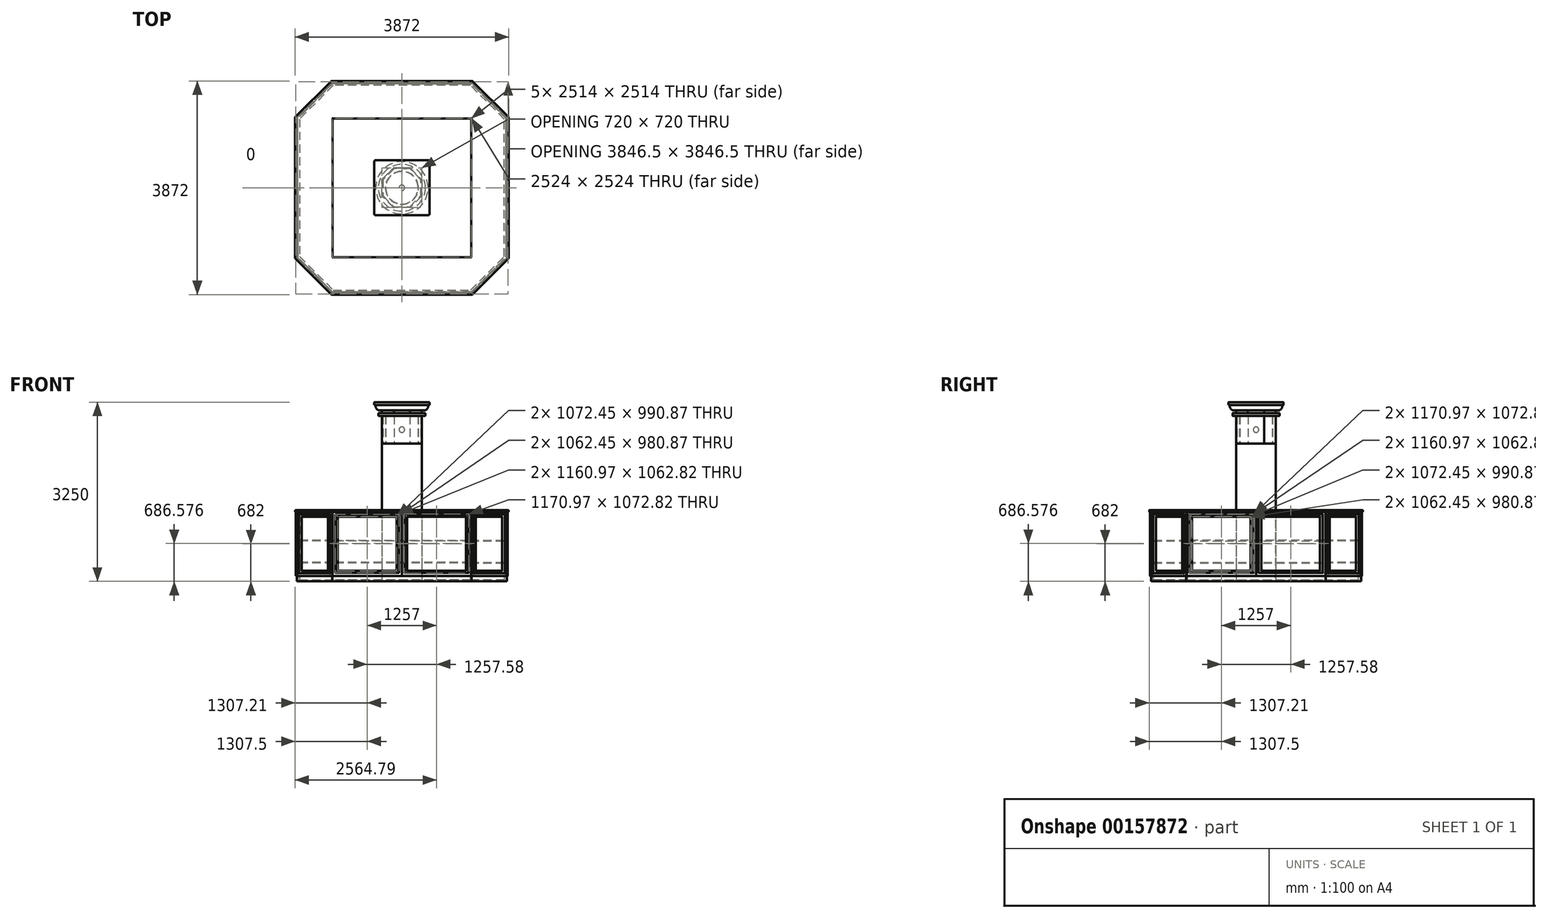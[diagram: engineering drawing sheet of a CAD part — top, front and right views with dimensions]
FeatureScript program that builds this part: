
annotation { "Feature Type Name" : "Feature", "Feature Type Description" : "" }
export const myFeature = defineFeature(function(context is Context, id is Id, definition is map)
    precondition{}
    {
        {
            var Q0;
            Q0=qCreatedBy(makeId("Top.planeOp"),FACE);
            var sketch = newSketch(context, id + "F0", { "sketchPlane" : qUnion([Q0])});
            skCircle(sketch, "E0.cCircle", {"center": v(0, 0) * mm, "radius": 360 * mm, "construction": true});
            skLineSegment(sketch, "E0.0", {"start": v(149.12, 360) * mm, "end": v(360, 149.12) * mm});
            skLineSegment(sketch, "E0.1", {"start": v(360, 149.12) * mm, "end": v(360, -149.12) * mm});
            skLineSegment(sketch, "E0.2", {"start": v(360, -149.12) * mm, "end": v(149.12, -360) * mm});
            skLineSegment(sketch, "E0.3", {"start": v(149.12, -360) * mm, "end": v(-149.12, -360) * mm});
            skLineSegment(sketch, "E0.4", {"start": v(-149.12, -360) * mm, "end": v(-360, -149.12) * mm});
            skLineSegment(sketch, "E0.5", {"start": v(-360, -149.12) * mm, "end": v(-360, 149.12) * mm});
            skLineSegment(sketch, "E0.6", {"start": v(-360, 149.12) * mm, "end": v(-149.12, 360) * mm});
            skLineSegment(sketch, "E0.7", {"start": v(-149.12, 360) * mm, "end": v(149.12, 360) * mm});
            skPoint(sketch, "E0.0.midPoint", {"position": v(254.56, 254.56) * mm});
            skLineSegment(sketch, "E1", {"start": v(0, 0) * mm, "end": v(360, 0) * mm, "construction": true});
            skSolve(sketch);
        }
        {
            var Q0;
            Q0=makeQuery(id+"F0.imprint","IMPRINT",FACE,{"disambiguationData":[TD([[makeQuery(id+"F0.imprint","IMPRINT",EDGE,{"derivedFrom":sQuery(id+"F0.wireOp",EDGE,"E0.0")}),-1.0]])]});
            var Q1;
            Q1=sQuery(id+"F0.wireOp",EDGE,"E1");
            extrude(context, id + "F1", {"entities" : qUnion([Q0]), "surfaceEntities" : qUnion([Q1]), "depth" : 3000 * mm});
        }
        {
            var Q0;
            Q0=qCreatedBy(makeId("Top.planeOp"),FACE);
            var sketch = newSketch(context, id + "F2", { "sketchPlane" : qUnion([Q0])});
            skLineSegment(sketch, "E2.bottom", {"start": v(1886, -1886) * mm, "end": v(-1886, -1886) * mm});
            skLineSegment(sketch, "E2.top", {"start": v(1886, 1886) * mm, "end": v(-1886, 1886) * mm});
            skLineSegment(sketch, "E2.left", {"start": v(1886, -1886) * mm, "end": v(1886, 1886) * mm});
            skLineSegment(sketch, "E2.right", {"start": v(-1886, -1886) * mm, "end": v(-1886, 1886) * mm});
            skPoint(sketch, "E2.middle", {"position": v(0, 0) * mm});
            skLineSegment(sketch, "E3.bottom", {"start": v(1257, -1257) * mm, "end": v(-1257, -1257) * mm});
            skLineSegment(sketch, "E3.top", {"start": v(1257, 1257) * mm, "end": v(-1257, 1257) * mm});
            skLineSegment(sketch, "E3.left", {"start": v(1257, -1257) * mm, "end": v(1257, 1257) * mm});
            skLineSegment(sketch, "E3.right", {"start": v(-1257, -1257) * mm, "end": v(-1257, 1257) * mm});
            skSolve(sketch);
        }
        {
            var Q0;
            Q0 = qSketchRegion(id + "F2", true);
            extrude(context, id + "F3", {"entities" : qUnion([Q0]), "depth" : 1264 * mm});
        }
        {
            var Q0;
            Q0=makeQuery(id+"F3.opExtrude","SWEPT_EDGE",EDGE,{"disambiguationData":[OSD([sQuery(id+"F2.wireOp",EDGE,"E2.top"),sQuery(id+"F2.wireOp",EDGE,"E2.right")])]});
            var Q1;
            Q1=makeQuery(id+"F3.opExtrude","SWEPT_EDGE",EDGE,{"disambiguationData":[OSD([sQuery(id+"F2.wireOp",EDGE,"E2.bottom"),sQuery(id+"F2.wireOp",EDGE,"E2.right")])]});
            var Q2;
            Q2=makeQuery(id+"F3.opExtrude","SWEPT_EDGE",EDGE,{"disambiguationData":[OSD([sQuery(id+"F2.wireOp",EDGE,"E2.bottom"),sQuery(id+"F2.wireOp",EDGE,"E2.left")])]});
            var Q3;
            Q3=makeQuery(id+"F3.opExtrude","SWEPT_EDGE",EDGE,{"disambiguationData":[OSD([sQuery(id+"F2.wireOp",EDGE,"E2.top"),sQuery(id+"F2.wireOp",EDGE,"E2.left")])]});
            chamfer(context, id + "F4", {"entities" : qUnion([Q0, Q1, Q2, Q3]), "width" : 629 * mm, "tangentPropagation" : true});
        }
        {
            var Q0;
            Q0=makeQuery(id+"F1.opExtrude","CAP_FACE",FACE,{"disambiguationData":[OSD([sQuery(id+"F0.wireOp",EDGE,"E0.0"),sQuery(id+"F0.wireOp",EDGE,"E0.1"),sQuery(id+"F0.wireOp",EDGE,"E0.2"),sQuery(id+"F0.wireOp",EDGE,"E0.3"),sQuery(id+"F0.wireOp",EDGE,"E0.4"),sQuery(id+"F0.wireOp",EDGE,"E0.5"),sQuery(id+"F0.wireOp",EDGE,"E0.6"),sQuery(id+"F0.wireOp",EDGE,"E0.7")])],"isStart":false});
            var sketch = newSketch(context, id + "F5", { "sketchPlane" : qUnion([Q0])});
            skCircle(sketch, "E4", {"center": v(0, 0) * mm, "radius": 425 * mm});
            skSolve(sketch);
        }
        {
            var Q0;
            Q0 = qSketchRegion(id + "F5", true);
            extrude(context, id + "F6", {"entities" : qUnion([Q0]), "operationType" : NewBodyOperationType.ADD, "depth" : 50 * mm});
        }
        {
            var Q0;
            Q0=makeQuery(id+"F6.opExtrude","CAP_FACE",FACE,{"disambiguationData":[OSD([sQuery(id+"F5.wireOp",EDGE,"E4")])],"isStart":false});
            var sketch = newSketch(context, id + "F7", { "sketchPlane" : qUnion([Q0])});
            skLineSegment(sketch, "E5.0.0", {"start": v(149.12, 360) * mm, "end": v(360, 149.12) * mm});
            skLineSegment(sketch, "E5.0.1", {"start": v(360, 149.12) * mm, "end": v(360, -149.12) * mm});
            skLineSegment(sketch, "E5.0.2", {"start": v(360, -149.12) * mm, "end": v(149.12, -360) * mm});
            skLineSegment(sketch, "E5.0.3", {"start": v(149.12, -360) * mm, "end": v(-149.12, -360) * mm});
            skLineSegment(sketch, "E5.0.4", {"start": v(-149.12, -360) * mm, "end": v(-360, -149.12) * mm});
            skLineSegment(sketch, "E5.0.5", {"start": v(-360, -149.12) * mm, "end": v(-360, 149.12) * mm});
            skLineSegment(sketch, "E5.0.6", {"start": v(-360, 149.12) * mm, "end": v(-149.12, 360) * mm});
            skLineSegment(sketch, "E5.0.7", {"start": v(-149.12, 360) * mm, "end": v(149.12, 360) * mm});
            skSolve(sketch);
        }
        {
            var Q0;
            Q0 = qSketchRegion(id + "F7", true);
            extrude(context, id + "F8", {"entities" : qUnion([Q0]), "operationType" : NewBodyOperationType.ADD, "depth" : 50 * mm});
        }
        {
            var Q0;
            Q0=makeQuery(id+"F8.opExtrude","CAP_FACE",FACE,{"disambiguationData":[OSD([sQuery(id+"F7.wireOp",EDGE,"E5.0.0"),sQuery(id+"F7.wireOp",EDGE,"E5.0.1"),sQuery(id+"F7.wireOp",EDGE,"E5.0.2"),sQuery(id+"F7.wireOp",EDGE,"E5.0.3"),sQuery(id+"F7.wireOp",EDGE,"E5.0.4"),sQuery(id+"F7.wireOp",EDGE,"E5.0.5"),sQuery(id+"F7.wireOp",EDGE,"E5.0.6"),sQuery(id+"F7.wireOp",EDGE,"E5.0.7")])],"isStart":false});
            var sketch = newSketch(context, id + "F9", { "sketchPlane" : qUnion([Q0])});
            skCircle(sketch, "E6", {"center": v(0, 0) * mm, "radius": 475 * mm});
            skSolve(sketch);
        }
        {
            var Q0;
            Q0 = qSketchRegion(id + "F9", true);
            extrude(context, id + "F10", {"entities" : qUnion([Q0]), "operationType" : NewBodyOperationType.ADD, "depth" : 100 * mm});
        }
        {
            var Q0;
            Q0=makeQuery(id+"F10.opExtrude","CAP_FACE",FACE,{"disambiguationData":[OSD([sQuery(id+"F9.wireOp",EDGE,"E6")])],"isStart":false});
            var sketch = newSketch(context, id + "F11", { "sketchPlane" : qUnion([Q0])});
            skLineSegment(sketch, "E7.bottom", {"start": v(500, -500) * mm, "end": v(-500, -500) * mm});
            skLineSegment(sketch, "E7.top", {"start": v(500, 500) * mm, "end": v(-500, 500) * mm});
            skLineSegment(sketch, "E7.left", {"start": v(500, -500) * mm, "end": v(500, 500) * mm});
            skLineSegment(sketch, "E7.right", {"start": v(-500, -500) * mm, "end": v(-500, 500) * mm});
            skPoint(sketch, "E7.middle", {"position": v(0, 0) * mm});
            skSolve(sketch);
        }
        {
            var Q0;
            Q0 = qSketchRegion(id + "F11", true);
            extrude(context, id + "F12", {"entities" : qUnion([Q0]), "operationType" : NewBodyOperationType.ADD, "depth" : 50 * mm});
        }
        {
            var Q0;
            Q0=makeQuery(id+"F10.opExtrude","CAP_EDGE",EDGE,{"disambiguationData":[OSD([sQuery(id+"F9.wireOp",EDGE,"E6")])],"isStart":true});
            fillet(context, id + "F13", {"entities" : qUnion([Q0]), "radius" : 75 * mm, "tangentPropagation" : true, "allowEdgeOverflow" : false});
        }
        {
            var Q0;
            Q0=makeQuery(id+"F12.opExtrude","SWEPT_EDGE",EDGE,{"disambiguationData":[OSD([sQuery(id+"F11.wireOp",EDGE,"E7.bottom"),sQuery(id+"F11.wireOp",EDGE,"E7.right")])]});
            var Q1;
            Q1=makeQuery(id+"F12.opExtrude","SWEPT_EDGE",EDGE,{"disambiguationData":[OSD([sQuery(id+"F11.wireOp",EDGE,"E7.bottom"),sQuery(id+"F11.wireOp",EDGE,"E7.left")])]});
            var Q2;
            Q2=makeQuery(id+"F12.opExtrude","SWEPT_EDGE",EDGE,{"disambiguationData":[OSD([sQuery(id+"F11.wireOp",EDGE,"E7.top"),sQuery(id+"F11.wireOp",EDGE,"E7.right")])]});
            var Q3;
            Q3=makeQuery(id+"F12.opExtrude","SWEPT_EDGE",EDGE,{"disambiguationData":[OSD([sQuery(id+"F11.wireOp",EDGE,"E7.top"),sQuery(id+"F11.wireOp",EDGE,"E7.left")])]});
            fillet(context, id + "F14", {"entities" : qUnion([Q0, Q1, Q2, Q3]), "radius" : 25 * mm, "tangentPropagation" : true, "allowEdgeOverflow" : false});
        }
        {
            var Q0;
            Q0=makeQuery(id+"F6.opExtrude","SWEPT_FACE",FACE,{"disambiguationData":[OSD([sQuery(id+"F5.wireOp",EDGE,"E4")])]});
            fillet(context, id + "F15", {"entities" : qUnion([Q0]), "radius" : 5 * mm, "tangentPropagation" : true, "allowEdgeOverflow" : false});
        }
        {
            var Q0;
            Q0=makeQuery(id+"F3.opExtrude","CAP_FACE",FACE,{"disambiguationData":[OSD([sQuery(id+"F2.wireOp",EDGE,"E2.bottom"),sQuery(id+"F2.wireOp",EDGE,"E2.top"),sQuery(id+"F2.wireOp",EDGE,"E2.left"),sQuery(id+"F2.wireOp",EDGE,"E2.right"),sQuery(id+"F2.wireOp",EDGE,"E3.bottom"),sQuery(id+"F2.wireOp",EDGE,"E3.top"),sQuery(id+"F2.wireOp",EDGE,"E3.left"),sQuery(id+"F2.wireOp",EDGE,"E3.right")])],"isStart":false});
            var sketch = newSketch(context, id + "F16", { "sketchPlane" : qUnion([Q0])});
            skLineSegment(sketch, "E8.0", {"start": v(1277.71, -1936) * mm, "end": v(1936, -1277.71) * mm});
            skLineSegment(sketch, "E8.1", {"start": v(1936, -1277.71) * mm, "end": v(1936, 1277.71) * mm});
            skLineSegment(sketch, "E8.2", {"start": v(1277.71, -1936) * mm, "end": v(-1277.71, -1936) * mm});
            skLineSegment(sketch, "E8.3", {"start": v(1936, 1277.71) * mm, "end": v(1277.71, 1936) * mm});
            skLineSegment(sketch, "E8.4", {"start": v(-1936, -1277.71) * mm, "end": v(-1277.71, -1936) * mm});
            skLineSegment(sketch, "E8.5", {"start": v(-1936, -1277.71) * mm, "end": v(-1936, 1277.71) * mm});
            skLineSegment(sketch, "E8.6", {"start": v(-1277.71, 1936) * mm, "end": v(-1936, 1277.71) * mm});
            skLineSegment(sketch, "E8.7", {"start": v(1277.71, 1936) * mm, "end": v(-1277.71, 1936) * mm});
            skLineSegment(sketch, "E9.0", {"start": v(1257, -1257) * mm, "end": v(1257, 1257) * mm});
            skLineSegment(sketch, "E9.1", {"start": v(1257, -1257) * mm, "end": v(-1257, -1257) * mm});
            skLineSegment(sketch, "E9.2", {"start": v(1257, 1257) * mm, "end": v(-1257, 1257) * mm});
            skLineSegment(sketch, "E9.3", {"start": v(-1257, -1257) * mm, "end": v(-1257, 1257) * mm});
            skSolve(sketch);
        }
        {
            var Q0;
            Q0=makeQuery(id+"F3.opExtrude","SWEPT_FACE",FACE,{"disambiguationData":[OSD([sQuery(id+"F2.wireOp",EDGE,"E3.top")])]});
            var Q1;
            Q1=makeQuery(id+"F3.opExtrude","SWEPT_FACE",FACE,{"disambiguationData":[OSD([sQuery(id+"F2.wireOp",EDGE,"E3.left")])]});
            var Q2;
            Q2=makeQuery(id+"F3.opExtrude","SWEPT_FACE",FACE,{"disambiguationData":[OSD([sQuery(id+"F2.wireOp",EDGE,"E3.bottom")])]});
            var Q3;
            Q3=makeQuery(id+"F3.opExtrude","SWEPT_FACE",FACE,{"disambiguationData":[OSD([sQuery(id+"F2.wireOp",EDGE,"E3.right")])]});
            shell(context, id + "F17", {"entities" : qUnion([Q0, Q1, Q2, Q3]), "thickness" : 30 * mm});
        }
        {
            var Q0;
            {var subQ0=sQuery(id+"F2.wireOp",EDGE,"E3.right");var subQ1=sQuery(id+"F2.wireOp",EDGE,"E3.left");var subQ2=sQuery(id+"F2.wireOp",EDGE,"E3.top");var subQ3=sQuery(id+"F2.wireOp",EDGE,"E3.bottom");var subQ4=sQuery(id+"F2.wireOp",EDGE,"E2.right");var subQ5=sQuery(id+"F2.wireOp",EDGE,"E2.left");var subQ6=sQuery(id+"F2.wireOp",EDGE,"E2.top");var subQ7=sQuery(id+"F2.wireOp",EDGE,"E2.bottom");Q0=makeQuery(id+"F17.opShell","OFFSET_FACE",FACE,{"disambiguationData":[OSD([subQ7,subQ6,subQ5,subQ4,subQ3,subQ2,subQ1,subQ0]),TDD([makeQuery(id+"F3.opExtrude","CAP_FACE",FACE,{"disambiguationData":[OSD([subQ7,subQ6,subQ5,subQ4,subQ3,subQ2,subQ1,subQ0])],"isStart":true})])]});}
            cPlane(context, id + "F18", {"entities" : qUnion([Q0]), "cplaneType" : CPlaneType.OFFSET, "offset" : 300 * mm, "width" : 150 * mm, "height" : 150 * mm});
        }
        {
            var Q0;
            Q0=qCreatedBy(id+"F18.planeOp",FACE);
            var sketch = newSketch(context, id + "F19", { "sketchPlane" : qUnion([Q0])});
            skLineSegment(sketch, "E10.0.0", {"start": v(1244.57, 1856) * mm, "end": v(-1244.57, 1856) * mm});
            skLineSegment(sketch, "E10.0.1", {"start": v(-1244.57, 1856) * mm, "end": v(-1856, 1244.57) * mm});
            skLineSegment(sketch, "E10.0.2", {"start": v(-1856, 1244.57) * mm, "end": v(-1856, -1244.57) * mm});
            skLineSegment(sketch, "E10.0.3", {"start": v(-1244.57, -1856) * mm, "end": v(-1856, -1244.57) * mm});
            skLineSegment(sketch, "E10.0.4", {"start": v(-1244.57, -1856) * mm, "end": v(1244.57, -1856) * mm});
            skLineSegment(sketch, "E10.0.5", {"start": v(1244.57, -1856) * mm, "end": v(1856, -1244.57) * mm});
            skLineSegment(sketch, "E10.0.6", {"start": v(1856, -1244.57) * mm, "end": v(1856, 1244.57) * mm});
            skLineSegment(sketch, "E10.0.7", {"start": v(1244.57, 1856) * mm, "end": v(1856, 1244.57) * mm});
            skLineSegment(sketch, "E11.0", {"start": v(1257, 1257) * mm, "end": v(-1257, 1257) * mm});
            skLineSegment(sketch, "E11.1", {"start": v(1257, -1257) * mm, "end": v(1257, 1257) * mm});
            skLineSegment(sketch, "E11.2", {"start": v(1257, -1257) * mm, "end": v(-1257, -1257) * mm});
            skLineSegment(sketch, "E11.3", {"start": v(-1257, -1257) * mm, "end": v(-1257, 1257) * mm});
            skSolve(sketch);
        }
        {
            var Q0;
            Q0 = qSketchRegion(id + "F19", true);
            extrude(context, id + "F20", {"entities" : qUnion([Q0]), "operationType" : NewBodyOperationType.ADD, "depth" : 15 * mm});
        }
        {
            var Q0;
            Q0=qCreatedBy(id+"F18.planeOp",FACE);
            cPlane(context, id + "F21", {"entities" : qUnion([Q0]), "cplaneType" : CPlaneType.OFFSET, "offset" : 400 * mm, "width" : 150 * mm, "height" : 150 * mm});
        }
        {
            var Q0;
            Q0=qCreatedBy(id+"F21.planeOp",FACE);
            var sketch = newSketch(context, id + "F22", { "sketchPlane" : qUnion([Q0])});
            skLineSegment(sketch, "E12.0.0", {"start": v(1856, 1244.57) * mm, "end": v(1244.57, 1856) * mm});
            skLineSegment(sketch, "E12.0.1", {"start": v(1244.57, 1856) * mm, "end": v(-1244.57, 1856) * mm});
            skLineSegment(sketch, "E12.0.2", {"start": v(-1244.57, 1856) * mm, "end": v(-1856, 1244.57) * mm});
            skLineSegment(sketch, "E12.0.3", {"start": v(-1856, 1244.57) * mm, "end": v(-1856, -1244.57) * mm});
            skLineSegment(sketch, "E12.0.4", {"start": v(-1856, -1244.57) * mm, "end": v(-1244.57, -1856) * mm});
            skLineSegment(sketch, "E12.0.5", {"start": v(-1244.57, -1856) * mm, "end": v(1244.57, -1856) * mm});
            skLineSegment(sketch, "E12.0.6", {"start": v(1244.57, -1856) * mm, "end": v(1856, -1244.57) * mm});
            skLineSegment(sketch, "E12.0.7", {"start": v(1856, -1244.57) * mm, "end": v(1856, 1244.57) * mm});
            skLineSegment(sketch, "E13.0", {"start": v(1257, 1257) * mm, "end": v(-1257, 1257) * mm});
            skLineSegment(sketch, "E13.1", {"start": v(1257, -1257) * mm, "end": v(1257, 1257) * mm});
            skLineSegment(sketch, "E13.2", {"start": v(1257, -1257) * mm, "end": v(-1257, -1257) * mm});
            skLineSegment(sketch, "E13.3", {"start": v(-1257, -1257) * mm, "end": v(-1257, 1257) * mm});
            skSolve(sketch);
        }
        {
            var Q0;
            Q0 = qSketchRegion(id + "F22", true);
            extrude(context, id + "F23", {"entities" : qUnion([Q0]), "operationType" : NewBodyOperationType.ADD, "depth" : 15 * mm});
        }
        {
            var Q0;
            Q0 = qSketchRegion(id + "F16", true);
            extrude(context, id + "F24", {"entities" : qUnion([Q0]), "depth" : 25 * mm});
        }
        {
            var Q0;
            Q0=makeQuery(id+"F3.opExtrude","CAP_FACE",FACE,{"disambiguationData":[OSD([sQuery(id+"F2.wireOp",EDGE,"E2.bottom"),sQuery(id+"F2.wireOp",EDGE,"E2.top"),sQuery(id+"F2.wireOp",EDGE,"E2.left"),sQuery(id+"F2.wireOp",EDGE,"E2.right"),sQuery(id+"F2.wireOp",EDGE,"E3.bottom"),sQuery(id+"F2.wireOp",EDGE,"E3.top"),sQuery(id+"F2.wireOp",EDGE,"E3.left"),sQuery(id+"F2.wireOp",EDGE,"E3.right")])],"isStart":true});
            var sketch = newSketch(context, id + "F25", { "sketchPlane" : qUnion([Q0])});
            skLineSegment(sketch, "E14.0", {"start": v(1257, 1257) * mm, "end": v(-1257, 1257) * mm});
            skLineSegment(sketch, "E14.1", {"start": v(1257, 1257) * mm, "end": v(1257, -1257) * mm});
            skLineSegment(sketch, "E14.2", {"start": v(1257, -1257) * mm, "end": v(-1257, -1257) * mm});
            skLineSegment(sketch, "E14.3", {"start": v(-1257, 1257) * mm, "end": v(-1257, -1257) * mm});
            skLineSegment(sketch, "E15.0", {"start": v(1906, 1265.28) * mm, "end": v(1906, -1265.28) * mm});
            skLineSegment(sketch, "E15.1", {"start": v(1265.28, -1906) * mm, "end": v(1906, -1265.28) * mm});
            skLineSegment(sketch, "E15.2", {"start": v(1906, 1265.28) * mm, "end": v(1265.28, 1906) * mm});
            skLineSegment(sketch, "E15.3", {"start": v(1265.28, -1906) * mm, "end": v(-1265.28, -1906) * mm});
            skLineSegment(sketch, "E15.4", {"start": v(1265.28, 1906) * mm, "end": v(-1265.28, 1906) * mm});
            skLineSegment(sketch, "E15.5", {"start": v(-1265.28, 1906) * mm, "end": v(-1906, 1265.28) * mm});
            skLineSegment(sketch, "E15.6", {"start": v(-1906, 1265.28) * mm, "end": v(-1906, -1265.28) * mm});
            skLineSegment(sketch, "E15.7", {"start": v(-1906, -1265.28) * mm, "end": v(-1265.28, -1906) * mm});
            skSolve(sketch);
        }
        {
            var Q0;
            Q0 = qSketchRegion(id + "F25", true);
            extrude(context, id + "F26", {"entities" : qUnion([Q0]), "oppositeDirection" : true, "depth" : 100 * mm});
        }
        {
            var Q0;
            Q0=makeQuery(id+"F6.opExtrude","CAP_FACE",FACE,{"disambiguationData":[OSD([sQuery(id+"F5.wireOp",EDGE,"E4")])],"isStart":true});
            var sketch = newSketch(context, id + "F27", { "sketchPlane" : qUnion([Q0])});
            skCircle(sketch, "E16.0", {"center": v(0, 0) * mm, "radius": 420 * mm});
            skSolve(sketch);
        }
        {
            var Q0;
            Q0 = qSketchRegion(id + "F27", true);
            extrude(context, id + "F28", {"entities" : qUnion([Q0]), "operationType" : NewBodyOperationType.REMOVE, "depth" : 500 * mm});
        }
        {
            var Q0;
            Q0=makeQuery(id+"F28.boolean.opBoolean","COPY",FACE,{"derivedFrom":makeQuery(id+"F28.opExtrude","CAP_FACE",FACE,{"disambiguationData":[OSD([sQuery(id+"F27.wireOp",EDGE,"E16.0")])],"isStart":false})});
            var sketch = newSketch(context, id + "F29", { "sketchPlane" : qUnion([Q0])});
            skCircle(sketch, "E17", {"center": v(0, 0) * mm, "radius": 300 * mm});
            skSolve(sketch);
        }
        {
            var Q0;
            Q0 = qSketchRegion(id + "F29", true);
            extrude(context, id + "F30", {"entities" : qUnion([Q0]), "depth" : 500 * mm});
        }
        {
            var Q0;
            Q0=makeQuery(id+"F30.opExtrude","CAP_FACE",FACE,{"disambiguationData":[OSD([sQuery(id+"F29.wireOp",EDGE,"E17")])],"isStart":true});
            var Q1;
            Q1=makeQuery(id+"F30.opExtrude","CAP_FACE",FACE,{"disambiguationData":[OSD([sQuery(id+"F29.wireOp",EDGE,"E17")])],"isStart":false});
            shell(context, id + "F31", {"entities" : qUnion([Q0, Q1]), "thickness" : 2 * mm});
        }
        {
            var Q0;
            Q0=makeQuery(id+"F28.boolean.opBoolean","COPY",FACE,{"derivedFrom":makeQuery(id+"F28.opExtrude","CAP_FACE",FACE,{"disambiguationData":[OSD([sQuery(id+"F27.wireOp",EDGE,"E16.0")])],"isStart":false})});
            var sketch = newSketch(context, id + "F32", { "sketchPlane" : qUnion([Q0])});
            skLineSegment(sketch, "E18.0", {"start": v(149.12, 360) * mm, "end": v(-149.12, 360) * mm});
            skLineSegment(sketch, "E19.0", {"start": v(-149.12, 360) * mm, "end": v(-360, 149.12) * mm});
            skLineSegment(sketch, "E20.0", {"start": v(-360, 149.12) * mm, "end": v(-360, -149.12) * mm});
            skLineSegment(sketch, "E21.0", {"start": v(360, 149.12) * mm, "end": v(149.12, 360) * mm});
            skLineSegment(sketch, "E22.0", {"start": v(360, -149.12) * mm, "end": v(360, 149.12) * mm});
            skLineSegment(sketch, "E23.0", {"start": v(149.12, -360) * mm, "end": v(360, -149.12) * mm});
            skLineSegment(sketch, "E24.0", {"start": v(-360, -149.12) * mm, "end": v(-149.12, -360) * mm});
            skLineSegment(sketch, "E25.0", {"start": v(-149.12, -360) * mm, "end": v(149.12, -360) * mm});
            skLineSegment(sketch, "E26.0", {"start": v(-345, 142.9) * mm, "end": v(-345, -142.9) * mm});
            skLineSegment(sketch, "E26.1", {"start": v(-142.9, 345) * mm, "end": v(-345, 142.9) * mm});
            skLineSegment(sketch, "E26.2", {"start": v(-345, -142.9) * mm, "end": v(-142.9, -345) * mm});
            skLineSegment(sketch, "E26.3", {"start": v(142.9, 345) * mm, "end": v(-142.9, 345) * mm});
            skLineSegment(sketch, "E26.4", {"start": v(-142.9, -345) * mm, "end": v(142.9, -345) * mm});
            skLineSegment(sketch, "E26.5", {"start": v(142.9, -345) * mm, "end": v(345, -142.9) * mm});
            skLineSegment(sketch, "E26.6", {"start": v(345, -142.9) * mm, "end": v(345, 142.9) * mm});
            skLineSegment(sketch, "E26.7", {"start": v(345, 142.9) * mm, "end": v(142.9, 345) * mm});
            skSolve(sketch);
        }
        {
            var Q0;
            Q0=makeQuery(id+"F32.imprint","IMPRINT",FACE,{"disambiguationData":[TD([[makeQuery(id+"F32.imprint","IMPRINT",EDGE,{"derivedFrom":sQuery(id+"F32.wireOp",EDGE,"E18.0")}),1.0]])]});
            extrude(context, id + "F33", {"entities" : qUnion([Q0]), "depth" : 500 * mm});
        }
        {
            var Q0;
            Q0=makeQuery(id+"F1.opExtrude","SWEPT_FACE",FACE,{"disambiguationData":[OSD([sQuery(id+"F0.wireOp",EDGE,"E0.7")])]});
            var sketch = newSketch(context, id + "F34", { "sketchPlane" : qUnion([Q0])});
            skLineSegment(sketch, "E27", {"start": v(-62.5, 2900) * mm, "end": v(-62.5, 100) * mm});
            skArc(sketch, "E28.0.startCap", {"start": v(-100, 2900) * mm, "mid": v(-62.5, 2937.5) * mm, "end": v(-25, 2900) * mm});
            skArc(sketch, "E28.0.endCap", {"start": v(-25, 100) * mm, "mid": v(-62.5, 62.5) * mm, "end": v(-100, 100) * mm});
            skLineSegment(sketch, "E28.0.left", {"start": v(-25, 2900) * mm, "end": v(-25, 100) * mm});
            skLineSegment(sketch, "E28.0.right", {"start": v(-100, 2900) * mm, "end": v(-100, 100) * mm});
            skSolve(sketch);
        }
        {
            var Q0;
            Q0 = qSketchRegion(id + "F34", true);
            extrude(context, id + "F35", {"entities" : qUnion([Q0]), "operationType" : NewBodyOperationType.REMOVE, "oppositeDirection" : true, "depth" : 10 * mm});
        }
        {
            var Q0;
            {var subQ0=sQuery(id+"F34.wireOp",EDGE,"E28.0.startCap");var subQ1=sQuery(id+"F34.wireOp",EDGE,"E28.0.right");Q0=makeQuery(id+"F35.boolean.opBoolean","COPY",EDGE,{"disambiguationData":[TD([makeQuery(id+"F35.opExtrude","SWEPT_FACE",FACE,{"disambiguationData":[OSD([subQ0])]})])],"derivedFrom":makeQuery(id+"F35.opExtrude","CAP_EDGE",EDGE,{"disambiguationData":[OSD([subQ1])],"isStart":false})});}
            var Q1;
            {var subQ0=sQuery(id+"F34.wireOp",EDGE,"E28.0.right");Q1=makeQuery(id+"F35.boolean.opBoolean","COPY",EDGE,{"disambiguationData":[TD([makeQuery(id+"F28.boolean.opBoolean","COPY",FACE,{"derivedFrom":makeQuery(id+"F28.opExtrude","CAP_FACE",FACE,{"disambiguationData":[OSD([sQuery(id+"F27.wireOp",EDGE,"E16.0")])],"isStart":false})})])],"derivedFrom":makeQuery(id+"F35.opExtrude","CAP_EDGE",EDGE,{"disambiguationData":[OSD([subQ0])],"isStart":false})});}
            fillet(context, id + "F36", {"entities" : qUnion([Q0, Q1]), "radius" : 10 * mm, "tangentPropagation" : true, "allowEdgeOverflow" : false});
        }
        {
            var Q0;
            Q0=qCreatedBy(makeId("Front.planeOp"),FACE);
            var sketch = newSketch(context, id + "F37", { "sketchPlane" : qUnion([Q0])});
            skLineSegment(sketch, "E29", {"start": v(0, 0) * mm, "end": v(0, 3766.95) * mm, "construction": true});
            skSolve(sketch);
        }
        {
            var Q0;
            Q0=qCreatedBy(makeId("Front.planeOp"),FACE);
            var sketch = newSketch(context, id + "F38", { "sketchPlane" : qUnion([Q0])});
            skArc(sketch, "E30", {"start": v(0, 2800) * mm, "mid": v(-50, 2750) * mm, "end": v(0, 2700) * mm});
            skLineSegment(sketch, "E31", {"start": v(0, 2800) * mm, "end": v(0, 2700) * mm});
            skSolve(sketch);
        }
        {
            var Q0;
            Q0=qCreatedBy(makeId("Front.planeOp"),FACE);
            var sketch = newSketch(context, id + "F39", { "sketchPlane" : qUnion([Q0])});
            skLineSegment(sketch, "E32", {"start": v(0, 2828.4) * mm, "end": v(0, 2674.55) * mm, "construction": true});
            skSolve(sketch);
        }
        {
            var Q0;
            Q0=makeQuery(id+"F38.imprint","IMPRINT",FACE,{"disambiguationData":[TD([[makeQuery(id+"F38.imprint","IMPRINT",EDGE,{"derivedFrom":sQuery(id+"F38.wireOp",EDGE,"E30")}),1.0]])]});
            var Q1;
            Q1=sQuery(id+"F39.wireOp",EDGE,"E32");
            revolve(context, id + "F40", {"entities" : qUnion([Q0]), "axis" : qUnion([Q1]), "revolveType" : RevolveType.FULL});
        }
        {
            var Q0;
            Q0=makeQuery(id+"F3.opExtrude","SWEPT_FACE",FACE,{"disambiguationData":[OSD([sQuery(id+"F2.wireOp",EDGE,"E2.left")])]});
            var sketch = newSketch(context, id + "F41", { "sketchPlane" : qUnion([Q0])});
            skLineSegment(sketch, "E33", {"start": v(0, 1264) * mm, "end": v(0, 100) * mm, "construction": true});
            skPoint(sketch, "E33.endSnap0", {"position": v(0, 1264) * mm});
            skLineSegment(sketch, "E34", {"start": v(0, 682) * mm, "end": v(-1257, 682) * mm, "construction": true});
            skLineSegment(sketch, "E35.bottom", {"start": v(0, 100) * mm, "end": v(-1257, 100) * mm});
            skLineSegment(sketch, "E35.top", {"start": v(0, 1264) * mm, "end": v(-1257, 1264) * mm});
            skLineSegment(sketch, "E35.left", {"start": v(0, 100) * mm, "end": v(0, 1264) * mm});
            skLineSegment(sketch, "E35.right", {"start": v(-1257, 100) * mm, "end": v(-1257, 1264) * mm});
            skPoint(sketch, "E35.middle", {"position": v(-628.5, 682) * mm});
            skLineSegment(sketch, "E36.bottom", {"start": v(-97.27, 191.57) * mm, "end": v(-1159.73, 191.57) * mm});
            skLineSegment(sketch, "E36.top", {"start": v(-97.27, 1172.43) * mm, "end": v(-1159.73, 1172.43) * mm});
            skLineSegment(sketch, "E36.left", {"start": v(-97.27, 191.57) * mm, "end": v(-97.27, 1172.43) * mm});
            skLineSegment(sketch, "E36.right", {"start": v(-1159.73, 191.57) * mm, "end": v(-1159.73, 1172.43) * mm});
            skSolve(sketch);
        }
        {
            var Q0;
            Q0 = qSketchRegion(id + "F41", true);
            extrude(context, id + "F42", {"entities" : qUnion([Q0]), "depth" : 10 * mm});
        }
        {
            var Q0;
            Q0=makeQuery(id+"F42.opExtrude","CAP_FACE",FACE,{"disambiguationData":[OSD([sQuery(id+"F41.wireOp",EDGE,"E35.bottom"),sQuery(id+"F41.wireOp",EDGE,"E35.top"),sQuery(id+"F41.wireOp",EDGE,"E35.left"),sQuery(id+"F41.wireOp",EDGE,"E35.right"),sQuery(id+"F41.wireOp",EDGE,"E36.bottom"),sQuery(id+"F41.wireOp",EDGE,"E36.top"),sQuery(id+"F41.wireOp",EDGE,"E36.left"),sQuery(id+"F41.wireOp",EDGE,"E36.right")])],"isStart":false});
            var sketch = newSketch(context, id + "F43", { "sketchPlane" : qUnion([Q0])});
            skLineSegment(sketch, "E37.bottom", {"start": v(-1257, 1264) * mm, "end": v(0, 1264) * mm});
            skLineSegment(sketch, "E37.top", {"start": v(-1257, 100) * mm, "end": v(0, 100) * mm});
            skLineSegment(sketch, "E37.left", {"start": v(-1257, 1264) * mm, "end": v(-1257, 100) * mm});
            skLineSegment(sketch, "E37.right", {"start": v(0, 1264) * mm, "end": v(0, 100) * mm});
            skLineSegment(sketch, "E38.bottom", {"start": v(-1209.28, 1217.98) * mm, "end": v(-48.3, 1217.98) * mm});
            skLineSegment(sketch, "E38.top", {"start": v(-1209.28, 155.17) * mm, "end": v(-48.3, 155.17) * mm});
            skLineSegment(sketch, "E38.left", {"start": v(-1209.28, 1217.98) * mm, "end": v(-1209.28, 155.17) * mm});
            skLineSegment(sketch, "E38.right", {"start": v(-48.3, 1217.98) * mm, "end": v(-48.3, 155.17) * mm});
            skSolve(sketch);
        }
        {
            var Q0;
            Q0 = qSketchRegion(id + "F43", true);
            extrude(context, id + "F44", {"entities" : qUnion([Q0]), "depth" : 25 * mm});
        }
        {
            var Q0;
            Q0=makeQuery(id+"F3.opExtrude","SWEPT_FACE",FACE,{"disambiguationData":[OSD([sQuery(id+"F2.wireOp",EDGE,"E2.left")])]});
            var sketch = newSketch(context, id + "F45", { "sketchPlane" : qUnion([Q0])});
            skLineSegment(sketch, "E39.0", {"start": v(-97.27, 1172.43) * mm, "end": v(-1159.73, 1172.43) * mm});
            skLineSegment(sketch, "E39.1", {"start": v(-1159.73, 191.57) * mm, "end": v(-1159.73, 1172.43) * mm});
            skLineSegment(sketch, "E39.2", {"start": v(-97.27, 191.57) * mm, "end": v(-97.27, 1172.43) * mm});
            skLineSegment(sketch, "E39.3", {"start": v(-97.27, 191.57) * mm, "end": v(-1159.73, 191.57) * mm});
            skSolve(sketch);
        }
        {
            var Q0;
            Q0 = qSketchRegion(id + "F45", true);
            extrude(context, id + "F46", {"entities" : qUnion([Q0]), "depth" : 5 * mm});
        }
        {
            var Q0;
            Q0=makeQuery(id+"F46.opExtrude","SWEPT_BODY",BODY,{"disambiguationData":[OSD([sQuery(id+"F45.wireOp",EDGE,"E39.0"),sQuery(id+"F45.wireOp",EDGE,"E39.1"),sQuery(id+"F45.wireOp",EDGE,"E39.2"),sQuery(id+"F45.wireOp",EDGE,"E39.3")])]});
            var Q1;
            Q1=makeQuery(id+"F42.opExtrude","SWEPT_BODY",BODY,{"disambiguationData":[OSD([sQuery(id+"F41.wireOp",EDGE,"E35.bottom"),sQuery(id+"F41.wireOp",EDGE,"E35.top"),sQuery(id+"F41.wireOp",EDGE,"E35.left"),sQuery(id+"F41.wireOp",EDGE,"E35.right"),sQuery(id+"F41.wireOp",EDGE,"E36.bottom"),sQuery(id+"F41.wireOp",EDGE,"E36.top"),sQuery(id+"F41.wireOp",EDGE,"E36.left"),sQuery(id+"F41.wireOp",EDGE,"E36.right")])]});
            var Q2;
            Q2=makeQuery(id+"F44.opExtrude","SWEPT_BODY",BODY,{"disambiguationData":[OSD([sQuery(id+"F43.wireOp",EDGE,"E37.bottom"),sQuery(id+"F43.wireOp",EDGE,"E37.top"),sQuery(id+"F43.wireOp",EDGE,"E37.left"),sQuery(id+"F43.wireOp",EDGE,"E37.right"),sQuery(id+"F43.wireOp",EDGE,"E38.bottom"),sQuery(id+"F43.wireOp",EDGE,"E38.top"),sQuery(id+"F43.wireOp",EDGE,"E38.left"),sQuery(id+"F43.wireOp",EDGE,"E38.right")])]});
            var Q3;
            Q3=qCreatedBy(makeId("Front.planeOp"),FACE);
            mirror(context, id + "F47", {"entities" : qUnion([Q0, Q1, Q2]), "mirrorPlane" : qUnion([Q3])});
        }
        {
            var Q0;
            Q0=qCreatedBy(makeId("Front.planeOp"),FACE);
            var sketch = newSketch(context, id + "F48", { "sketchPlane" : qUnion([Q0])});
            skLineSegment(sketch, "E40", {"start": v(0, 3551.4) * mm, "end": v(0, -1302.8) * mm, "construction": true});
            skSolve(sketch);
        }
        {
            var Q0;
            Q0=makeQuery(id+"F46.opExtrude","SWEPT_BODY",BODY,{"disambiguationData":[OSD([sQuery(id+"F45.wireOp",EDGE,"E39.0"),sQuery(id+"F45.wireOp",EDGE,"E39.1"),sQuery(id+"F45.wireOp",EDGE,"E39.2"),sQuery(id+"F45.wireOp",EDGE,"E39.3")])]});
            var Q1;
            Q1=makeQuery(id+"F42.opExtrude","SWEPT_BODY",BODY,{"disambiguationData":[OSD([sQuery(id+"F41.wireOp",EDGE,"E35.bottom"),sQuery(id+"F41.wireOp",EDGE,"E35.top"),sQuery(id+"F41.wireOp",EDGE,"E35.left"),sQuery(id+"F41.wireOp",EDGE,"E35.right"),sQuery(id+"F41.wireOp",EDGE,"E36.bottom"),sQuery(id+"F41.wireOp",EDGE,"E36.top"),sQuery(id+"F41.wireOp",EDGE,"E36.left"),sQuery(id+"F41.wireOp",EDGE,"E36.right")])]});
            var Q2;
            Q2=makeQuery(id+"F44.opExtrude","SWEPT_BODY",BODY,{"disambiguationData":[OSD([sQuery(id+"F43.wireOp",EDGE,"E37.bottom"),sQuery(id+"F43.wireOp",EDGE,"E37.top"),sQuery(id+"F43.wireOp",EDGE,"E37.left"),sQuery(id+"F43.wireOp",EDGE,"E37.right"),sQuery(id+"F43.wireOp",EDGE,"E38.bottom"),sQuery(id+"F43.wireOp",EDGE,"E38.top"),sQuery(id+"F43.wireOp",EDGE,"E38.left"),sQuery(id+"F43.wireOp",EDGE,"E38.right")])]});
            var Q3;
            Q3=makeQuery(id+"F47.opPattern","COPY",BODY,{"derivedFrom":makeQuery(id+"F44.opExtrude","SWEPT_BODY",BODY,{"disambiguationData":[OSD([sQuery(id+"F43.wireOp",EDGE,"E37.bottom"),sQuery(id+"F43.wireOp",EDGE,"E37.top"),sQuery(id+"F43.wireOp",EDGE,"E37.left"),sQuery(id+"F43.wireOp",EDGE,"E37.right"),sQuery(id+"F43.wireOp",EDGE,"E38.bottom"),sQuery(id+"F43.wireOp",EDGE,"E38.top"),sQuery(id+"F43.wireOp",EDGE,"E38.left"),sQuery(id+"F43.wireOp",EDGE,"E38.right")])]}),"instanceName":"1"});
            var Q4;
            Q4=makeQuery(id+"F47.opPattern","COPY",BODY,{"derivedFrom":makeQuery(id+"F42.opExtrude","SWEPT_BODY",BODY,{"disambiguationData":[OSD([sQuery(id+"F41.wireOp",EDGE,"E35.bottom"),sQuery(id+"F41.wireOp",EDGE,"E35.top"),sQuery(id+"F41.wireOp",EDGE,"E35.left"),sQuery(id+"F41.wireOp",EDGE,"E35.right"),sQuery(id+"F41.wireOp",EDGE,"E36.bottom"),sQuery(id+"F41.wireOp",EDGE,"E36.top"),sQuery(id+"F41.wireOp",EDGE,"E36.left"),sQuery(id+"F41.wireOp",EDGE,"E36.right")])]}),"instanceName":"1"});
            var Q5;
            Q5=makeQuery(id+"F47.opPattern","COPY",BODY,{"derivedFrom":makeQuery(id+"F46.opExtrude","SWEPT_BODY",BODY,{"disambiguationData":[OSD([sQuery(id+"F45.wireOp",EDGE,"E39.0"),sQuery(id+"F45.wireOp",EDGE,"E39.1"),sQuery(id+"F45.wireOp",EDGE,"E39.2"),sQuery(id+"F45.wireOp",EDGE,"E39.3")])]}),"instanceName":"1"});
            var Q6;
            Q6=sQuery(id+"F48.wireOp",EDGE,"E40");
            circularPattern(context, id + "F49", {"entities" : qUnion([Q0, Q1, Q2, Q3, Q4, Q5]), "axis" : qUnion([Q6]), "angle" : 360 * degree, "instanceCount" : 4, "equalSpace" : true});
        }
        {
            var Q0;
            Q0=makeQuery(id+"F4.opChamfer","BLEND_FACE",FACE,{"disambiguationData":[OSD([sQuery(id+"F2.wireOp",EDGE,"E2.bottom"),sQuery(id+"F2.wireOp",EDGE,"E2.left")])]});
            var sketch = newSketch(context, id + "F50", { "sketchPlane" : qUnion([Q0])});
            skLineSegment(sketch, "E41.bottom", {"start": v(-444.77, 1264) * mm, "end": v(444.77, 1264) * mm});
            skLineSegment(sketch, "E41.top", {"start": v(-444.77, 100) * mm, "end": v(444.77, 100) * mm});
            skLineSegment(sketch, "E41.left", {"start": v(-444.77, 1264) * mm, "end": v(-444.77, 100) * mm});
            skLineSegment(sketch, "E41.right", {"start": v(444.77, 1264) * mm, "end": v(444.77, 100) * mm});
            skLineSegment(sketch, "E42.bottom", {"start": v(337.74, 191.57) * mm, "end": v(-337.74, 191.57) * mm});
            skLineSegment(sketch, "E42.top", {"start": v(337.74, 1172.43) * mm, "end": v(-337.74, 1172.43) * mm});
            skLineSegment(sketch, "E42.left", {"start": v(337.74, 191.57) * mm, "end": v(337.74, 1172.43) * mm});
            skLineSegment(sketch, "E42.right", {"start": v(-337.74, 191.57) * mm, "end": v(-337.74, 1172.43) * mm});
            skPoint(sketch, "E42.middle", {"position": v(0, 682) * mm});
            skPoint(sketch, "E42.middle.positionSnap0", {"position": v(0, 1264) * mm});
            skPoint(sketch, "E42.middle.positionSnap1", {"position": v(-444.77, 682) * mm});
            skPoint(sketch, "E42.centerSnap0", {"position": v(0, 1264) * mm});
            skPoint(sketch, "E42.centerSnap1", {"position": v(-444.77, 682) * mm});
            skSolve(sketch);
        }
        {
            var Q0;
            Q0 = qSketchRegion(id + "F50", true);
            extrude(context, id + "F51", {"entities" : qUnion([Q0]), "depth" : 10 * mm});
        }
        {
            var Q0;
            Q0=makeQuery(id+"F51.opExtrude","CAP_FACE",FACE,{"disambiguationData":[OSD([sQuery(id+"F50.wireOp",EDGE,"E41.bottom"),sQuery(id+"F50.wireOp",EDGE,"E41.top"),sQuery(id+"F50.wireOp",EDGE,"E41.left"),sQuery(id+"F50.wireOp",EDGE,"E41.right"),sQuery(id+"F50.wireOp",EDGE,"E42.bottom"),sQuery(id+"F50.wireOp",EDGE,"E42.top"),sQuery(id+"F50.wireOp",EDGE,"E42.left"),sQuery(id+"F50.wireOp",EDGE,"E42.right")])],"isStart":false});
            var sketch = newSketch(context, id + "F52", { "sketchPlane" : qUnion([Q0])});
            skLineSegment(sketch, "E43.0", {"start": v(-444.77, 100) * mm, "end": v(-444.77, 1264) * mm});
            skLineSegment(sketch, "E43.1", {"start": v(-444.77, 1264) * mm, "end": v(444.77, 1264) * mm});
            skLineSegment(sketch, "E43.2", {"start": v(444.77, 1264) * mm, "end": v(444.77, 100) * mm});
            skLineSegment(sketch, "E43.3", {"start": v(-444.77, 100) * mm, "end": v(444.77, 100) * mm});
            skLineSegment(sketch, "E44.bottom", {"start": v(403.74, 146.02) * mm, "end": v(-403.74, 146.02) * mm});
            skLineSegment(sketch, "E44.top", {"start": v(403.74, 1217.98) * mm, "end": v(-403.74, 1217.98) * mm});
            skLineSegment(sketch, "E44.left", {"start": v(403.74, 146.02) * mm, "end": v(403.74, 1217.98) * mm});
            skLineSegment(sketch, "E44.right", {"start": v(-403.74, 146.02) * mm, "end": v(-403.74, 1217.98) * mm});
            skPoint(sketch, "E44.middle", {"position": v(0, 682) * mm});
            skPoint(sketch, "E44.middle.positionSnap0", {"position": v(-337.74, 682) * mm});
            skPoint(sketch, "E44.centerSnap0", {"position": v(-337.74, 682) * mm});
            skSolve(sketch);
        }
        {
            var Q0;
            Q0 = qSketchRegion(id + "F52", true);
            extrude(context, id + "F53", {"entities" : qUnion([Q0]), "depth" : 25 * mm});
        }
        {
            var Q0;
            Q0=makeQuery(id+"F4.opChamfer","BLEND_FACE",FACE,{"disambiguationData":[OSD([sQuery(id+"F2.wireOp",EDGE,"E2.bottom"),sQuery(id+"F2.wireOp",EDGE,"E2.left")])]});
            var sketch = newSketch(context, id + "F54", { "sketchPlane" : qUnion([Q0])});
            skLineSegment(sketch, "E45.0", {"start": v(337.74, 1172.43) * mm, "end": v(-337.74, 1172.43) * mm});
            skLineSegment(sketch, "E46.0", {"start": v(-337.74, 191.57) * mm, "end": v(-337.74, 1172.43) * mm});
            skLineSegment(sketch, "E47.0", {"start": v(337.74, 191.57) * mm, "end": v(337.74, 1172.43) * mm});
            skLineSegment(sketch, "E48.0", {"start": v(337.74, 191.57) * mm, "end": v(-337.74, 191.57) * mm});
            skSolve(sketch);
        }
        {
            var Q0;
            Q0 = qSketchRegion(id + "F54", true);
            extrude(context, id + "F55", {"entities" : qUnion([Q0]), "depth" : 5 * mm});
        }
        {
            var Q0;
            Q0=makeQuery(id+"F53.opExtrude","CAP_FACE",FACE,{"disambiguationData":[OSD([sQuery(id+"F52.wireOp",EDGE,"E43.0"),sQuery(id+"F52.wireOp",EDGE,"E43.1"),sQuery(id+"F52.wireOp",EDGE,"E43.2"),sQuery(id+"F52.wireOp",EDGE,"E43.3"),sQuery(id+"F52.wireOp",EDGE,"E44.bottom"),sQuery(id+"F52.wireOp",EDGE,"E44.top"),sQuery(id+"F52.wireOp",EDGE,"E44.left"),sQuery(id+"F52.wireOp",EDGE,"E44.right")])],"isStart":false});
            var Q1;
            Q1=makeQuery(id+"F51.opExtrude","CAP_FACE",FACE,{"disambiguationData":[OSD([sQuery(id+"F50.wireOp",EDGE,"E41.bottom"),sQuery(id+"F50.wireOp",EDGE,"E41.top"),sQuery(id+"F50.wireOp",EDGE,"E41.left"),sQuery(id+"F50.wireOp",EDGE,"E41.right"),sQuery(id+"F50.wireOp",EDGE,"E42.bottom"),sQuery(id+"F50.wireOp",EDGE,"E42.top"),sQuery(id+"F50.wireOp",EDGE,"E42.left"),sQuery(id+"F50.wireOp",EDGE,"E42.right")])],"isStart":false});
            var Q2;
            Q2=makeQuery(id+"F49.opPattern","COPY",FACE,{"derivedFrom":makeQuery(id+"F47.opPattern","COPY",FACE,{"derivedFrom":makeQuery(id+"F42.opExtrude","CAP_FACE",FACE,{"disambiguationData":[OSD([sQuery(id+"F41.wireOp",EDGE,"E35.bottom"),sQuery(id+"F41.wireOp",EDGE,"E35.top"),sQuery(id+"F41.wireOp",EDGE,"E35.left"),sQuery(id+"F41.wireOp",EDGE,"E35.right"),sQuery(id+"F41.wireOp",EDGE,"E36.bottom"),sQuery(id+"F41.wireOp",EDGE,"E36.top"),sQuery(id+"F41.wireOp",EDGE,"E36.left"),sQuery(id+"F41.wireOp",EDGE,"E36.right")])],"isStart":false}),"instanceName":"1"}),"instanceName":"1"});
            var Q3;
            Q3=makeQuery(id+"F49.opPattern","COPY",FACE,{"derivedFrom":makeQuery(id+"F47.opPattern","COPY",FACE,{"derivedFrom":makeQuery(id+"F44.opExtrude","CAP_FACE",FACE,{"disambiguationData":[OSD([sQuery(id+"F43.wireOp",EDGE,"E37.bottom"),sQuery(id+"F43.wireOp",EDGE,"E37.top"),sQuery(id+"F43.wireOp",EDGE,"E37.left"),sQuery(id+"F43.wireOp",EDGE,"E37.right"),sQuery(id+"F43.wireOp",EDGE,"E38.bottom"),sQuery(id+"F43.wireOp",EDGE,"E38.top"),sQuery(id+"F43.wireOp",EDGE,"E38.left"),sQuery(id+"F43.wireOp",EDGE,"E38.right")])],"isStart":false}),"instanceName":"1"}),"instanceName":"1"});
            var Q4;
            Q4=makeQuery(id+"F49.opPattern","COPY",EDGE,{"derivedFrom":makeQuery(id+"F47.opPattern","COPY",EDGE,{"derivedFrom":makeQuery(id+"F44.opExtrude","CAP_EDGE",EDGE,{"disambiguationData":[OSD([sQuery(id+"F43.wireOp",EDGE,"E37.right")])],"isStart":false}),"instanceName":"1"}),"instanceName":"1"});
            var Q5;
            Q5=makeQuery(id+"F49.opPattern","COPY",FACE,{"derivedFrom":makeQuery(id+"F42.opExtrude","CAP_FACE",FACE,{"disambiguationData":[OSD([sQuery(id+"F41.wireOp",EDGE,"E35.bottom"),sQuery(id+"F41.wireOp",EDGE,"E35.top"),sQuery(id+"F41.wireOp",EDGE,"E35.left"),sQuery(id+"F41.wireOp",EDGE,"E35.right"),sQuery(id+"F41.wireOp",EDGE,"E36.bottom"),sQuery(id+"F41.wireOp",EDGE,"E36.top"),sQuery(id+"F41.wireOp",EDGE,"E36.left"),sQuery(id+"F41.wireOp",EDGE,"E36.right")])],"isStart":false}),"instanceName":"1"});
            var Q6;
            Q6=makeQuery(id+"F49.opPattern","COPY",FACE,{"derivedFrom":makeQuery(id+"F47.opPattern","COPY",FACE,{"derivedFrom":makeQuery(id+"F44.opExtrude","CAP_FACE",FACE,{"disambiguationData":[OSD([sQuery(id+"F43.wireOp",EDGE,"E37.bottom"),sQuery(id+"F43.wireOp",EDGE,"E37.top"),sQuery(id+"F43.wireOp",EDGE,"E37.left"),sQuery(id+"F43.wireOp",EDGE,"E37.right"),sQuery(id+"F43.wireOp",EDGE,"E38.bottom"),sQuery(id+"F43.wireOp",EDGE,"E38.top"),sQuery(id+"F43.wireOp",EDGE,"E38.left"),sQuery(id+"F43.wireOp",EDGE,"E38.right")])],"isStart":false}),"instanceName":"1"}),"instanceName":"2"});
            var Q7;
            Q7=makeQuery(id+"F49.opPattern","COPY",FACE,{"derivedFrom":makeQuery(id+"F47.opPattern","COPY",FACE,{"derivedFrom":makeQuery(id+"F42.opExtrude","CAP_FACE",FACE,{"disambiguationData":[OSD([sQuery(id+"F41.wireOp",EDGE,"E35.bottom"),sQuery(id+"F41.wireOp",EDGE,"E35.top"),sQuery(id+"F41.wireOp",EDGE,"E35.left"),sQuery(id+"F41.wireOp",EDGE,"E35.right"),sQuery(id+"F41.wireOp",EDGE,"E36.bottom"),sQuery(id+"F41.wireOp",EDGE,"E36.top"),sQuery(id+"F41.wireOp",EDGE,"E36.left"),sQuery(id+"F41.wireOp",EDGE,"E36.right")])],"isStart":false}),"instanceName":"1"}),"instanceName":"2"});
            var Q8;
            Q8=makeQuery(id+"F49.opPattern","COPY",FACE,{"derivedFrom":makeQuery(id+"F42.opExtrude","CAP_FACE",FACE,{"disambiguationData":[OSD([sQuery(id+"F41.wireOp",EDGE,"E35.bottom"),sQuery(id+"F41.wireOp",EDGE,"E35.top"),sQuery(id+"F41.wireOp",EDGE,"E35.left"),sQuery(id+"F41.wireOp",EDGE,"E35.right"),sQuery(id+"F41.wireOp",EDGE,"E36.bottom"),sQuery(id+"F41.wireOp",EDGE,"E36.top"),sQuery(id+"F41.wireOp",EDGE,"E36.left"),sQuery(id+"F41.wireOp",EDGE,"E36.right")])],"isStart":false}),"instanceName":"2"});
            var Q9;
            Q9=makeQuery(id+"F49.opPattern","COPY",FACE,{"derivedFrom":makeQuery(id+"F44.opExtrude","CAP_FACE",FACE,{"disambiguationData":[OSD([sQuery(id+"F43.wireOp",EDGE,"E37.bottom"),sQuery(id+"F43.wireOp",EDGE,"E37.top"),sQuery(id+"F43.wireOp",EDGE,"E37.left"),sQuery(id+"F43.wireOp",EDGE,"E37.right"),sQuery(id+"F43.wireOp",EDGE,"E38.bottom"),sQuery(id+"F43.wireOp",EDGE,"E38.top"),sQuery(id+"F43.wireOp",EDGE,"E38.left"),sQuery(id+"F43.wireOp",EDGE,"E38.right")])],"isStart":false}),"instanceName":"2"});
            var Q10;
            Q10=makeQuery(id+"F49.opPattern","COPY",FACE,{"derivedFrom":makeQuery(id+"F47.opPattern","COPY",FACE,{"derivedFrom":makeQuery(id+"F44.opExtrude","CAP_FACE",FACE,{"disambiguationData":[OSD([sQuery(id+"F43.wireOp",EDGE,"E37.bottom"),sQuery(id+"F43.wireOp",EDGE,"E37.top"),sQuery(id+"F43.wireOp",EDGE,"E37.left"),sQuery(id+"F43.wireOp",EDGE,"E37.right"),sQuery(id+"F43.wireOp",EDGE,"E38.bottom"),sQuery(id+"F43.wireOp",EDGE,"E38.top"),sQuery(id+"F43.wireOp",EDGE,"E38.left"),sQuery(id+"F43.wireOp",EDGE,"E38.right")])],"isStart":false}),"instanceName":"1"}),"instanceName":"3"});
            var Q11;
            Q11=makeQuery(id+"F49.opPattern","COPY",FACE,{"derivedFrom":makeQuery(id+"F47.opPattern","COPY",FACE,{"derivedFrom":makeQuery(id+"F42.opExtrude","CAP_FACE",FACE,{"disambiguationData":[OSD([sQuery(id+"F41.wireOp",EDGE,"E35.bottom"),sQuery(id+"F41.wireOp",EDGE,"E35.top"),sQuery(id+"F41.wireOp",EDGE,"E35.left"),sQuery(id+"F41.wireOp",EDGE,"E35.right"),sQuery(id+"F41.wireOp",EDGE,"E36.bottom"),sQuery(id+"F41.wireOp",EDGE,"E36.top"),sQuery(id+"F41.wireOp",EDGE,"E36.left"),sQuery(id+"F41.wireOp",EDGE,"E36.right")])],"isStart":false}),"instanceName":"1"}),"instanceName":"3"});
            var Q12;
            Q12=makeQuery(id+"F49.opPattern","COPY",FACE,{"derivedFrom":makeQuery(id+"F42.opExtrude","CAP_FACE",FACE,{"disambiguationData":[OSD([sQuery(id+"F41.wireOp",EDGE,"E35.bottom"),sQuery(id+"F41.wireOp",EDGE,"E35.top"),sQuery(id+"F41.wireOp",EDGE,"E35.left"),sQuery(id+"F41.wireOp",EDGE,"E35.right"),sQuery(id+"F41.wireOp",EDGE,"E36.bottom"),sQuery(id+"F41.wireOp",EDGE,"E36.top"),sQuery(id+"F41.wireOp",EDGE,"E36.left"),sQuery(id+"F41.wireOp",EDGE,"E36.right")])],"isStart":false}),"instanceName":"3"});
            var Q13;
            Q13=makeQuery(id+"F49.opPattern","COPY",FACE,{"derivedFrom":makeQuery(id+"F44.opExtrude","CAP_FACE",FACE,{"disambiguationData":[OSD([sQuery(id+"F43.wireOp",EDGE,"E37.bottom"),sQuery(id+"F43.wireOp",EDGE,"E37.top"),sQuery(id+"F43.wireOp",EDGE,"E37.left"),sQuery(id+"F43.wireOp",EDGE,"E37.right"),sQuery(id+"F43.wireOp",EDGE,"E38.bottom"),sQuery(id+"F43.wireOp",EDGE,"E38.top"),sQuery(id+"F43.wireOp",EDGE,"E38.left"),sQuery(id+"F43.wireOp",EDGE,"E38.right")])],"isStart":false}),"instanceName":"3"});
            var Q14;
            Q14=makeQuery(id+"F42.opExtrude","CAP_FACE",FACE,{"disambiguationData":[OSD([sQuery(id+"F41.wireOp",EDGE,"E35.bottom"),sQuery(id+"F41.wireOp",EDGE,"E35.top"),sQuery(id+"F41.wireOp",EDGE,"E35.left"),sQuery(id+"F41.wireOp",EDGE,"E35.right"),sQuery(id+"F41.wireOp",EDGE,"E36.bottom"),sQuery(id+"F41.wireOp",EDGE,"E36.top"),sQuery(id+"F41.wireOp",EDGE,"E36.left"),sQuery(id+"F41.wireOp",EDGE,"E36.right")])],"isStart":false});
            var Q15;
            Q15=makeQuery(id+"F44.opExtrude","CAP_FACE",FACE,{"disambiguationData":[OSD([sQuery(id+"F43.wireOp",EDGE,"E37.bottom"),sQuery(id+"F43.wireOp",EDGE,"E37.top"),sQuery(id+"F43.wireOp",EDGE,"E37.left"),sQuery(id+"F43.wireOp",EDGE,"E37.right"),sQuery(id+"F43.wireOp",EDGE,"E38.bottom"),sQuery(id+"F43.wireOp",EDGE,"E38.top"),sQuery(id+"F43.wireOp",EDGE,"E38.left"),sQuery(id+"F43.wireOp",EDGE,"E38.right")])],"isStart":false});
            var Q16;
            Q16=makeQuery(id+"F47.opPattern","COPY",FACE,{"derivedFrom":makeQuery(id+"F44.opExtrude","CAP_FACE",FACE,{"disambiguationData":[OSD([sQuery(id+"F43.wireOp",EDGE,"E37.bottom"),sQuery(id+"F43.wireOp",EDGE,"E37.top"),sQuery(id+"F43.wireOp",EDGE,"E37.left"),sQuery(id+"F43.wireOp",EDGE,"E37.right"),sQuery(id+"F43.wireOp",EDGE,"E38.bottom"),sQuery(id+"F43.wireOp",EDGE,"E38.top"),sQuery(id+"F43.wireOp",EDGE,"E38.left"),sQuery(id+"F43.wireOp",EDGE,"E38.right")])],"isStart":false}),"instanceName":"1"});
            var Q17;
            Q17=makeQuery(id+"F47.opPattern","COPY",FACE,{"derivedFrom":makeQuery(id+"F42.opExtrude","CAP_FACE",FACE,{"disambiguationData":[OSD([sQuery(id+"F41.wireOp",EDGE,"E35.bottom"),sQuery(id+"F41.wireOp",EDGE,"E35.top"),sQuery(id+"F41.wireOp",EDGE,"E35.left"),sQuery(id+"F41.wireOp",EDGE,"E35.right"),sQuery(id+"F41.wireOp",EDGE,"E36.bottom"),sQuery(id+"F41.wireOp",EDGE,"E36.top"),sQuery(id+"F41.wireOp",EDGE,"E36.left"),sQuery(id+"F41.wireOp",EDGE,"E36.right")])],"isStart":false}),"instanceName":"1"});
            var Q18;
            Q18=makeQuery(id+"F24.opExtrude","CAP_FACE",FACE,{"disambiguationData":[OSD([sQuery(id+"F16.wireOp",EDGE,"E8.0"),sQuery(id+"F16.wireOp",EDGE,"E8.1"),sQuery(id+"F16.wireOp",EDGE,"E8.2"),sQuery(id+"F16.wireOp",EDGE,"E8.3"),sQuery(id+"F16.wireOp",EDGE,"E8.4"),sQuery(id+"F16.wireOp",EDGE,"E8.5"),sQuery(id+"F16.wireOp",EDGE,"E8.6"),sQuery(id+"F16.wireOp",EDGE,"E8.7"),sQuery(id+"F16.wireOp",EDGE,"E9.0"),sQuery(id+"F16.wireOp",EDGE,"E9.1"),sQuery(id+"F16.wireOp",EDGE,"E9.2"),sQuery(id+"F16.wireOp",EDGE,"E9.3")])],"isStart":false});
            var Q19;
            Q19=makeQuery(id+"F24.opExtrude","CAP_FACE",FACE,{"disambiguationData":[OSD([sQuery(id+"F16.wireOp",EDGE,"E8.0"),sQuery(id+"F16.wireOp",EDGE,"E8.1"),sQuery(id+"F16.wireOp",EDGE,"E8.2"),sQuery(id+"F16.wireOp",EDGE,"E8.3"),sQuery(id+"F16.wireOp",EDGE,"E8.4"),sQuery(id+"F16.wireOp",EDGE,"E8.5"),sQuery(id+"F16.wireOp",EDGE,"E8.6"),sQuery(id+"F16.wireOp",EDGE,"E8.7"),sQuery(id+"F16.wireOp",EDGE,"E9.0"),sQuery(id+"F16.wireOp",EDGE,"E9.1"),sQuery(id+"F16.wireOp",EDGE,"E9.2"),sQuery(id+"F16.wireOp",EDGE,"E9.3")])],"isStart":true});
            var Q20;
            Q20=makeQuery(id+"F12.opExtrude","CAP_FACE",FACE,{"disambiguationData":[OSD([sQuery(id+"F11.wireOp",EDGE,"E7.bottom"),sQuery(id+"F11.wireOp",EDGE,"E7.top"),sQuery(id+"F11.wireOp",EDGE,"E7.left"),sQuery(id+"F11.wireOp",EDGE,"E7.right")])],"isStart":false});
            fillet(context, id + "F56", {"entities" : qUnion([Q0, Q1, Q2, Q3, Q4, Q5, Q6, Q7, Q8, Q9, Q10, Q11, Q12, Q13, Q14, Q15, Q16, Q17, Q18, Q19, Q20]), "radius" : 5 * mm, "tangentPropagation" : true, "allowEdgeOverflow" : false});
        }
        {
            var Q0;
            Q0=makeQuery(id+"F51.opExtrude","SWEPT_BODY",BODY,{"disambiguationData":[OSD([sQuery(id+"F50.wireOp",EDGE,"E41.bottom"),sQuery(id+"F50.wireOp",EDGE,"E41.top"),sQuery(id+"F50.wireOp",EDGE,"E41.left"),sQuery(id+"F50.wireOp",EDGE,"E41.right"),sQuery(id+"F50.wireOp",EDGE,"E42.bottom"),sQuery(id+"F50.wireOp",EDGE,"E42.top"),sQuery(id+"F50.wireOp",EDGE,"E42.left"),sQuery(id+"F50.wireOp",EDGE,"E42.right")])]});
            var Q1;
            Q1=makeQuery(id+"F53.opExtrude","SWEPT_BODY",BODY,{"disambiguationData":[OSD([sQuery(id+"F52.wireOp",EDGE,"E43.0"),sQuery(id+"F52.wireOp",EDGE,"E43.1"),sQuery(id+"F52.wireOp",EDGE,"E43.2"),sQuery(id+"F52.wireOp",EDGE,"E43.3"),sQuery(id+"F52.wireOp",EDGE,"E44.bottom"),sQuery(id+"F52.wireOp",EDGE,"E44.top"),sQuery(id+"F52.wireOp",EDGE,"E44.left"),sQuery(id+"F52.wireOp",EDGE,"E44.right")])]});
            var Q2;
            Q2=makeQuery(id+"F55.opExtrude","SWEPT_BODY",BODY,{"disambiguationData":[OSD([sQuery(id+"F54.wireOp",EDGE,"E45.0"),sQuery(id+"F54.wireOp",EDGE,"E46.0"),sQuery(id+"F54.wireOp",EDGE,"E47.0"),sQuery(id+"F54.wireOp",EDGE,"E48.0")])]});
            var Q3;
            Q3=sQuery(id+"F48.wireOp",EDGE,"E40");
            circularPattern(context, id + "F57", {"entities" : qUnion([Q0, Q1, Q2]), "axis" : qUnion([Q3]), "angle" : 360 * degree, "instanceCount" : 4, "equalSpace" : true});
        }
        {
            var Q0;
            Q0=makeQuery(id+"F24.opExtrude","CAP_FACE",FACE,{"disambiguationData":[OSD([sQuery(id+"F16.wireOp",EDGE,"E8.0"),sQuery(id+"F16.wireOp",EDGE,"E8.1"),sQuery(id+"F16.wireOp",EDGE,"E8.2"),sQuery(id+"F16.wireOp",EDGE,"E8.3"),sQuery(id+"F16.wireOp",EDGE,"E8.4"),sQuery(id+"F16.wireOp",EDGE,"E8.5"),sQuery(id+"F16.wireOp",EDGE,"E8.6"),sQuery(id+"F16.wireOp",EDGE,"E8.7"),sQuery(id+"F16.wireOp",EDGE,"E9.0"),sQuery(id+"F16.wireOp",EDGE,"E9.1"),sQuery(id+"F16.wireOp",EDGE,"E9.2"),sQuery(id+"F16.wireOp",EDGE,"E9.3")])],"isStart":true});
            var sketch = newSketch(context, id + "F58", { "sketchPlane" : qUnion([Q0])});
            skLineSegment(sketch, "E49.0", {"start": v(1272.43, -1923.25) * mm, "end": v(1923.25, -1272.43) * mm});
            skLineSegment(sketch, "E49.1", {"start": v(-1272.43, -1923.25) * mm, "end": v(1272.43, -1923.25) * mm});
            skLineSegment(sketch, "E49.2", {"start": v(1923.25, -1272.43) * mm, "end": v(1923.25, 1272.43) * mm});
            skLineSegment(sketch, "E49.3", {"start": v(-1923.25, -1272.43) * mm, "end": v(-1272.43, -1923.25) * mm});
            skLineSegment(sketch, "E49.4", {"start": v(1923.25, 1272.43) * mm, "end": v(1272.43, 1923.25) * mm});
            skLineSegment(sketch, "E49.5", {"start": v(1272.43, 1923.25) * mm, "end": v(-1272.43, 1923.25) * mm});
            skLineSegment(sketch, "E49.6", {"start": v(-1272.43, 1923.25) * mm, "end": v(-1923.25, 1272.43) * mm});
            skLineSegment(sketch, "E49.7", {"start": v(-1923.25, 1272.43) * mm, "end": v(-1923.25, -1272.43) * mm});
            skLineSegment(sketch, "E50.0", {"start": v(1274.4, -1928) * mm, "end": v(1928, -1274.4) * mm});
            skLineSegment(sketch, "E50.1", {"start": v(-1274.4, -1928) * mm, "end": v(1274.4, -1928) * mm});
            skLineSegment(sketch, "E50.2", {"start": v(1928, -1274.4) * mm, "end": v(1928, 1274.4) * mm});
            skLineSegment(sketch, "E50.3", {"start": v(-1928, -1274.4) * mm, "end": v(-1274.4, -1928) * mm});
            skLineSegment(sketch, "E50.4", {"start": v(1928, 1274.4) * mm, "end": v(1274.4, 1928) * mm});
            skLineSegment(sketch, "E50.5", {"start": v(1274.4, 1928) * mm, "end": v(-1274.4, 1928) * mm});
            skLineSegment(sketch, "E50.6", {"start": v(-1274.4, 1928) * mm, "end": v(-1928, 1274.4) * mm});
            skLineSegment(sketch, "E50.7", {"start": v(-1928, 1274.4) * mm, "end": v(-1928, -1274.4) * mm});
            skSolve(sketch);
        }
        {
            var Q0;
            Q0 = qSketchRegion(id + "F58", true);
            extrude(context, id + "F59", {"entities" : qUnion([Q0]), "depth" : 2.5 * mm});
        }
        {
            var Q0;
            Q0=makeQuery(id+"F28.boolean.opBoolean","COPY",FACE,{"derivedFrom":makeQuery(id+"F28.opExtrude","CAP_FACE",FACE,{"disambiguationData":[OSD([sQuery(id+"F27.wireOp",EDGE,"E16.0")])],"isStart":false})});
            var sketch = newSketch(context, id + "F60", { "sketchPlane" : qUnion([Q0])});
            skCircle(sketch, "E51.0", {"center": v(0, 0) * mm, "radius": 293 * mm});
            skSolve(sketch);
        }
        {
            var Q0;
            Q0=makeQuery(id+"F60.imprint","IMPRINT",FACE,{"disambiguationData":[TD([[makeQuery(id+"F60.imprint","IMPRINT",EDGE,{"derivedFrom":sQuery(id+"F60.wireOp",EDGE,"E51.0")}),1.0]])]});
            extrude(context, id + "F61", {"entities" : qUnion([Q0]), "depth" : 500 * mm});
        }
        {
            var Q0;
            {var subQ0=sQuery(id+"F34.wireOp",EDGE,"E28.0.right");Q0=makeQuery(id+"F9qVh1xIXOQniXD_4.4.F36.opFillet","BLEND_EDGE",EDGE,{"blendedFrom":[makeQuery(id+"F9qVh1xIXOQniXD_4.4.F35.boolean.opBoolean","COPY",EDGE,{"disambiguationData":[TD([makeQuery(id+"F28.boolean.opBoolean","COPY",FACE,{"derivedFrom":makeQuery(id+"F28.opExtrude","CAP_FACE",FACE,{"disambiguationData":[OSD([sQuery(id+"F27.wireOp",EDGE,"E16.0")])],"isStart":false})})])],"derivedFrom":makeQuery(id+"F9qVh1xIXOQniXD_4.4.F35.opExtrude","CAP_EDGE",EDGE,{"disambiguationData":[OSD([subQ0])],"isStart":false})}),makeQuery(id+"F1.opExtrude","SWEPT_FACE",FACE,{"disambiguationData":[OSD([sQuery(id+"F0.wireOp",EDGE,"E0.3")])]})],"blendedInto":[makeQuery(id+"F1.opExtrude","SWEPT_FACE",FACE,{"disambiguationData":[OSD([sQuery(id+"F0.wireOp",EDGE,"E0.3")])]})]});}
            var Q1;
            {var subQ1=sQuery(id+"F34.wireOp",EDGE,"E28.0.left");Q1=makeQuery(id+"F9qVh1xIXOQniXD_4.4.FJxHqB9KzhM7FEk_4.1.F36.opFillet","BLEND_EDGE",EDGE,{"blendedFrom":[makeQuery(id+"F9qVh1xIXOQniXD_4.4.FJxHqB9KzhM7FEk_4.1.F35.boolean.opBoolean","COPY",EDGE,{"disambiguationData":[TD([makeQuery(id+"F28.boolean.opBoolean","COPY",FACE,{"derivedFrom":makeQuery(id+"F28.opExtrude","CAP_FACE",FACE,{"disambiguationData":[OSD([sQuery(id+"F27.wireOp",EDGE,"E16.0")])],"isStart":false})})])],"derivedFrom":makeQuery(id+"F9qVh1xIXOQniXD_4.4.FJxHqB9KzhM7FEk_4.1.F35.opExtrude","CAP_EDGE",EDGE,{"disambiguationData":[OSD([subQ1])],"isStart":false})}),makeQuery(id+"F1.opExtrude","SWEPT_FACE",FACE,{"disambiguationData":[OSD([sQuery(id+"F0.wireOp",EDGE,"E0.3")])]})],"blendedInto":[makeQuery(id+"F1.opExtrude","SWEPT_FACE",FACE,{"disambiguationData":[OSD([sQuery(id+"F0.wireOp",EDGE,"E0.3")])]})]});}
            var Q2;
            Q2=makeQuery(id+"F1.opExtrude","SWEPT_EDGE",EDGE,{"disambiguationData":[OSD([sQuery(id+"F0.wireOp",EDGE,"E0.2"),sQuery(id+"F0.wireOp",EDGE,"E0.3")])]});
            var Q3;
            {var subQ1=sQuery(id+"F34.wireOp",EDGE,"E28.0.right");Q3=makeQuery(id+"F9qVh1xIXOQniXD_4.5.F36.opFillet","BLEND_EDGE",EDGE,{"blendedFrom":[makeQuery(id+"F9qVh1xIXOQniXD_4.5.F35.boolean.opBoolean","COPY",EDGE,{"disambiguationData":[TD([makeQuery(id+"F28.boolean.opBoolean","COPY",FACE,{"derivedFrom":makeQuery(id+"F28.opExtrude","CAP_FACE",FACE,{"disambiguationData":[OSD([sQuery(id+"F27.wireOp",EDGE,"E16.0")])],"isStart":false})})])],"derivedFrom":makeQuery(id+"F9qVh1xIXOQniXD_4.5.F35.opExtrude","CAP_EDGE",EDGE,{"disambiguationData":[OSD([subQ1])],"isStart":false})}),makeQuery(id+"F1.opExtrude","SWEPT_FACE",FACE,{"disambiguationData":[OSD([sQuery(id+"F0.wireOp",EDGE,"E0.2")])]})],"blendedInto":[makeQuery(id+"F1.opExtrude","SWEPT_FACE",FACE,{"disambiguationData":[OSD([sQuery(id+"F0.wireOp",EDGE,"E0.2")])]})]});}
            var Q4;
            {var subQ1=sQuery(id+"F34.wireOp",EDGE,"E28.0.left");Q4=makeQuery(id+"F9qVh1xIXOQniXD_4.5.F36.opFillet","BLEND_EDGE",EDGE,{"blendedFrom":[makeQuery(id+"F9qVh1xIXOQniXD_4.5.F35.boolean.opBoolean","COPY",EDGE,{"disambiguationData":[TD([makeQuery(id+"F28.boolean.opBoolean","COPY",FACE,{"derivedFrom":makeQuery(id+"F28.opExtrude","CAP_FACE",FACE,{"disambiguationData":[OSD([sQuery(id+"F27.wireOp",EDGE,"E16.0")])],"isStart":false})})])],"derivedFrom":makeQuery(id+"F9qVh1xIXOQniXD_4.5.F35.opExtrude","CAP_EDGE",EDGE,{"disambiguationData":[OSD([subQ1])],"isStart":false})}),makeQuery(id+"F1.opExtrude","SWEPT_FACE",FACE,{"disambiguationData":[OSD([sQuery(id+"F0.wireOp",EDGE,"E0.2")])]})],"blendedInto":[makeQuery(id+"F1.opExtrude","SWEPT_FACE",FACE,{"disambiguationData":[OSD([sQuery(id+"F0.wireOp",EDGE,"E0.2")])]})]});}
            var Q5;
            {var subQ0=sQuery(id+"F34.wireOp",EDGE,"E28.0.left");Q5=makeQuery(id+"F9qVh1xIXOQniXD_4.3.FJxHqB9KzhM7FEk_4.1.F36.opFillet","BLEND_EDGE",EDGE,{"blendedFrom":[makeQuery(id+"F9qVh1xIXOQniXD_4.3.FJxHqB9KzhM7FEk_4.1.F35.boolean.opBoolean","COPY",EDGE,{"disambiguationData":[TD([makeQuery(id+"F28.boolean.opBoolean","COPY",FACE,{"derivedFrom":makeQuery(id+"F28.opExtrude","CAP_FACE",FACE,{"disambiguationData":[OSD([sQuery(id+"F27.wireOp",EDGE,"E16.0")])],"isStart":false})})])],"derivedFrom":makeQuery(id+"F9qVh1xIXOQniXD_4.3.FJxHqB9KzhM7FEk_4.1.F35.opExtrude","CAP_EDGE",EDGE,{"disambiguationData":[OSD([subQ0])],"isStart":false})}),makeQuery(id+"F1.opExtrude","SWEPT_FACE",FACE,{"disambiguationData":[OSD([sQuery(id+"F0.wireOp",EDGE,"E0.2")])]})],"blendedInto":[makeQuery(id+"F1.opExtrude","SWEPT_FACE",FACE,{"disambiguationData":[OSD([sQuery(id+"F0.wireOp",EDGE,"E0.2")])]})]});}
            var Q6;
            Q6=makeQuery(id+"F1.opExtrude","SWEPT_EDGE",EDGE,{"disambiguationData":[OSD([sQuery(id+"F0.wireOp",EDGE,"E0.1"),sQuery(id+"F0.wireOp",EDGE,"E0.2")])]});
            var Q7;
            Q7=makeQuery(id+"F1.opExtrude","SWEPT_EDGE",EDGE,{"disambiguationData":[OSD([sQuery(id+"F0.wireOp",EDGE,"E0.3"),sQuery(id+"F0.wireOp",EDGE,"E0.4")])]});
            var Q8;
            {var subQ0=sQuery(id+"F34.wireOp",EDGE,"E28.0.right");Q8=makeQuery(id+"F9qVh1xIXOQniXD_4.5.FJxHqB9KzhM7FEk_4.1.F36.opFillet","BLEND_EDGE",EDGE,{"blendedFrom":[makeQuery(id+"F9qVh1xIXOQniXD_4.5.FJxHqB9KzhM7FEk_4.1.F35.boolean.opBoolean","COPY",EDGE,{"disambiguationData":[TD([makeQuery(id+"F28.boolean.opBoolean","COPY",FACE,{"derivedFrom":makeQuery(id+"F28.opExtrude","CAP_FACE",FACE,{"disambiguationData":[OSD([sQuery(id+"F27.wireOp",EDGE,"E16.0")])],"isStart":false})})])],"derivedFrom":makeQuery(id+"F9qVh1xIXOQniXD_4.5.FJxHqB9KzhM7FEk_4.1.F35.opExtrude","CAP_EDGE",EDGE,{"disambiguationData":[OSD([subQ0])],"isStart":false})}),makeQuery(id+"F1.opExtrude","SWEPT_FACE",FACE,{"disambiguationData":[OSD([sQuery(id+"F0.wireOp",EDGE,"E0.4")])]})],"blendedInto":[makeQuery(id+"F1.opExtrude","SWEPT_FACE",FACE,{"disambiguationData":[OSD([sQuery(id+"F0.wireOp",EDGE,"E0.4")])]})]});}
            var Q9;
            {var subQ0=makeQuery(id+"F28.boolean.opBoolean","COPY",FACE,{"derivedFrom":makeQuery(id+"F28.opExtrude","CAP_FACE",FACE,{"disambiguationData":[OSD([sQuery(id+"F27.wireOp",EDGE,"E16.0")])],"isStart":false})});var subQ1=sQuery(id+"F34.wireOp",EDGE,"E28.0.endCap");var subQ3=sQuery(id+"F34.wireOp",EDGE,"E28.0.left");var subQ5=sQuery(id+"F34.wireOp",EDGE,"E28.0.right");var subQ6=makeQuery(id+"F9qVh1xIXOQniXD_4.3.F35.opExtrude","CAP_FACE",FACE,{"disambiguationData":[OSD([sQuery(id+"F34.wireOp",EDGE,"E28.0.startCap"),subQ1,subQ3,subQ5])],"isStart":false});Q9=makeQuery(id+"F9qVh1xIXOQniXD_4.3.F36.opFillet","BLEND_EDGE",EDGE,{"blendedFrom":[makeQuery(id+"F9qVh1xIXOQniXD_4.3.F35.boolean.opBoolean","COPY",EDGE,{"disambiguationData":[TD([subQ0])],"derivedFrom":makeQuery(id+"F9qVh1xIXOQniXD_4.3.F35.opExtrude","CAP_EDGE",EDGE,{"disambiguationData":[OSD([subQ3])],"isStart":false})}),makeQuery(id+"F9qVh1xIXOQniXD_4.3.F35.boolean.opBoolean","COPY",FACE,{"disambiguationData":[TD([subQ0])],"derivedFrom":subQ6})],"blendedInto":[makeQuery(id+"F9qVh1xIXOQniXD_4.3.F35.boolean.opBoolean","COPY",FACE,{"disambiguationData":[TD([subQ0])],"derivedFrom":subQ6})]});}
            var Q10;
            {var subQ0=sQuery(id+"F34.wireOp",EDGE,"E28.0.right");Q10=makeQuery(id+"F9qVh1xIXOQniXD_4.3.F36.opFillet","BLEND_EDGE",EDGE,{"blendedFrom":[makeQuery(id+"F9qVh1xIXOQniXD_4.3.F35.boolean.opBoolean","COPY",EDGE,{"disambiguationData":[TD([makeQuery(id+"F28.boolean.opBoolean","COPY",FACE,{"derivedFrom":makeQuery(id+"F28.opExtrude","CAP_FACE",FACE,{"disambiguationData":[OSD([sQuery(id+"F27.wireOp",EDGE,"E16.0")])],"isStart":false})})])],"derivedFrom":makeQuery(id+"F9qVh1xIXOQniXD_4.3.F35.opExtrude","CAP_EDGE",EDGE,{"disambiguationData":[OSD([subQ0])],"isStart":false})}),makeQuery(id+"F1.opExtrude","SWEPT_FACE",FACE,{"disambiguationData":[OSD([sQuery(id+"F0.wireOp",EDGE,"E0.4")])]})],"blendedInto":[makeQuery(id+"F1.opExtrude","SWEPT_FACE",FACE,{"disambiguationData":[OSD([sQuery(id+"F0.wireOp",EDGE,"E0.4")])]})]});}
            var Q11;
            Q11=makeQuery(id+"F1.opExtrude","SWEPT_EDGE",EDGE,{"disambiguationData":[OSD([sQuery(id+"F0.wireOp",EDGE,"E0.4"),sQuery(id+"F0.wireOp",EDGE,"E0.5")])]});
            var Q12;
            {var subQ0=sQuery(id+"F34.wireOp",EDGE,"E28.0.right");Q12=makeQuery(id+"F9qVh1xIXOQniXD_4.6.FJxHqB9KzhM7FEk_4.1.F36.opFillet","BLEND_EDGE",EDGE,{"blendedFrom":[makeQuery(id+"F9qVh1xIXOQniXD_4.6.FJxHqB9KzhM7FEk_4.1.F35.boolean.opBoolean","COPY",EDGE,{"disambiguationData":[TD([makeQuery(id+"F28.boolean.opBoolean","COPY",FACE,{"derivedFrom":makeQuery(id+"F28.opExtrude","CAP_FACE",FACE,{"disambiguationData":[OSD([sQuery(id+"F27.wireOp",EDGE,"E16.0")])],"isStart":false})})])],"derivedFrom":makeQuery(id+"F9qVh1xIXOQniXD_4.6.FJxHqB9KzhM7FEk_4.1.F35.opExtrude","CAP_EDGE",EDGE,{"disambiguationData":[OSD([subQ0])],"isStart":false})}),makeQuery(id+"F1.opExtrude","SWEPT_FACE",FACE,{"disambiguationData":[OSD([sQuery(id+"F0.wireOp",EDGE,"E0.5")])]})],"blendedInto":[makeQuery(id+"F1.opExtrude","SWEPT_FACE",FACE,{"disambiguationData":[OSD([sQuery(id+"F0.wireOp",EDGE,"E0.5")])]})]});}
            var Q13;
            {var subQ0=sQuery(id+"F34.wireOp",EDGE,"E28.0.left");Q13=makeQuery(id+"F9qVh1xIXOQniXD_4.2.F36.opFillet","BLEND_EDGE",EDGE,{"blendedFrom":[makeQuery(id+"F9qVh1xIXOQniXD_4.2.F35.boolean.opBoolean","COPY",EDGE,{"disambiguationData":[TD([makeQuery(id+"F28.boolean.opBoolean","COPY",FACE,{"derivedFrom":makeQuery(id+"F28.opExtrude","CAP_FACE",FACE,{"disambiguationData":[OSD([sQuery(id+"F27.wireOp",EDGE,"E16.0")])],"isStart":false})})])],"derivedFrom":makeQuery(id+"F9qVh1xIXOQniXD_4.2.F35.opExtrude","CAP_EDGE",EDGE,{"disambiguationData":[OSD([subQ0])],"isStart":false})}),makeQuery(id+"F1.opExtrude","SWEPT_FACE",FACE,{"disambiguationData":[OSD([sQuery(id+"F0.wireOp",EDGE,"E0.5")])]})],"blendedInto":[makeQuery(id+"F1.opExtrude","SWEPT_FACE",FACE,{"disambiguationData":[OSD([sQuery(id+"F0.wireOp",EDGE,"E0.5")])]})]});}
            var Q14;
            Q14=makeQuery(id+"F1.opExtrude","SWEPT_EDGE",EDGE,{"disambiguationData":[OSD([sQuery(id+"F0.wireOp",EDGE,"E0.5"),sQuery(id+"F0.wireOp",EDGE,"E0.6")])]});
            var Q15;
            {var subQ0=sQuery(id+"F34.wireOp",EDGE,"E28.0.left");Q15=makeQuery(id+"F9qVh1xIXOQniXD_4.7.FJxHqB9KzhM7FEk_4.1.F36.opFillet","BLEND_EDGE",EDGE,{"blendedFrom":[makeQuery(id+"F9qVh1xIXOQniXD_4.7.FJxHqB9KzhM7FEk_4.1.F35.boolean.opBoolean","COPY",EDGE,{"disambiguationData":[TD([makeQuery(id+"F28.boolean.opBoolean","COPY",FACE,{"derivedFrom":makeQuery(id+"F28.opExtrude","CAP_FACE",FACE,{"disambiguationData":[OSD([sQuery(id+"F27.wireOp",EDGE,"E16.0")])],"isStart":false})})])],"derivedFrom":makeQuery(id+"F9qVh1xIXOQniXD_4.7.FJxHqB9KzhM7FEk_4.1.F35.opExtrude","CAP_EDGE",EDGE,{"disambiguationData":[OSD([subQ0])],"isStart":false})}),makeQuery(id+"F1.opExtrude","SWEPT_FACE",FACE,{"disambiguationData":[OSD([sQuery(id+"F0.wireOp",EDGE,"E0.6")])]})],"blendedInto":[makeQuery(id+"F1.opExtrude","SWEPT_FACE",FACE,{"disambiguationData":[OSD([sQuery(id+"F0.wireOp",EDGE,"E0.6")])]})]});}
            var Q16;
            {var subQ0=sQuery(id+"F34.wireOp",EDGE,"E28.0.left");Q16=makeQuery(id+"F9qVh1xIXOQniXD_4.1.F36.opFillet","BLEND_EDGE",EDGE,{"blendedFrom":[makeQuery(id+"F9qVh1xIXOQniXD_4.1.F35.boolean.opBoolean","COPY",EDGE,{"disambiguationData":[TD([makeQuery(id+"F28.boolean.opBoolean","COPY",FACE,{"derivedFrom":makeQuery(id+"F28.opExtrude","CAP_FACE",FACE,{"disambiguationData":[OSD([sQuery(id+"F27.wireOp",EDGE,"E16.0")])],"isStart":false})})])],"derivedFrom":makeQuery(id+"F9qVh1xIXOQniXD_4.1.F35.opExtrude","CAP_EDGE",EDGE,{"disambiguationData":[OSD([subQ0])],"isStart":false})}),makeQuery(id+"F1.opExtrude","SWEPT_FACE",FACE,{"disambiguationData":[OSD([sQuery(id+"F0.wireOp",EDGE,"E0.6")])]})],"blendedInto":[makeQuery(id+"F1.opExtrude","SWEPT_FACE",FACE,{"disambiguationData":[OSD([sQuery(id+"F0.wireOp",EDGE,"E0.6")])]})]});}
            var Q17;
            Q17=makeQuery(id+"F1.opExtrude","SWEPT_EDGE",EDGE,{"disambiguationData":[OSD([sQuery(id+"F0.wireOp",EDGE,"E0.6"),sQuery(id+"F0.wireOp",EDGE,"E0.7")])]});
            var Q18;
            {var subQ0=sQuery(id+"F34.wireOp",EDGE,"E28.0.right");Q18=makeQuery(id+"FJxHqB9KzhM7FEk_4.1.F36.opFillet","BLEND_EDGE",EDGE,{"blendedFrom":[makeQuery(id+"FJxHqB9KzhM7FEk_4.1.F35.boolean.opBoolean","COPY",EDGE,{"disambiguationData":[TD([makeQuery(id+"F28.boolean.opBoolean","COPY",FACE,{"derivedFrom":makeQuery(id+"F28.opExtrude","CAP_FACE",FACE,{"disambiguationData":[OSD([sQuery(id+"F27.wireOp",EDGE,"E16.0")])],"isStart":false})})])],"derivedFrom":makeQuery(id+"FJxHqB9KzhM7FEk_4.1.F35.opExtrude","CAP_EDGE",EDGE,{"disambiguationData":[OSD([subQ0])],"isStart":false})}),makeQuery(id+"F1.opExtrude","SWEPT_FACE",FACE,{"disambiguationData":[OSD([sQuery(id+"F0.wireOp",EDGE,"E0.7")])]})],"blendedInto":[makeQuery(id+"F1.opExtrude","SWEPT_FACE",FACE,{"disambiguationData":[OSD([sQuery(id+"F0.wireOp",EDGE,"E0.7")])]})]});}
            var Q19;
            {var subQ0=sQuery(id+"F34.wireOp",EDGE,"E28.0.left");Q19=makeQuery(id+"F36.opFillet","BLEND_EDGE",EDGE,{"blendedFrom":[makeQuery(id+"F35.boolean.opBoolean","COPY",EDGE,{"disambiguationData":[TD([makeQuery(id+"F28.boolean.opBoolean","COPY",FACE,{"derivedFrom":makeQuery(id+"F28.opExtrude","CAP_FACE",FACE,{"disambiguationData":[OSD([sQuery(id+"F27.wireOp",EDGE,"E16.0")])],"isStart":false})})])],"derivedFrom":makeQuery(id+"F35.opExtrude","CAP_EDGE",EDGE,{"disambiguationData":[OSD([subQ0])],"isStart":false})}),makeQuery(id+"F1.opExtrude","SWEPT_FACE",FACE,{"disambiguationData":[OSD([sQuery(id+"F0.wireOp",EDGE,"E0.7")])]})],"blendedInto":[makeQuery(id+"F1.opExtrude","SWEPT_FACE",FACE,{"disambiguationData":[OSD([sQuery(id+"F0.wireOp",EDGE,"E0.7")])]})]});}
            var Q20;
            Q20=makeQuery(id+"F1.opExtrude","SWEPT_EDGE",EDGE,{"disambiguationData":[OSD([sQuery(id+"F0.wireOp",EDGE,"E0.0"),sQuery(id+"F0.wireOp",EDGE,"E0.7")])]});
            var Q21;
            {var subQ0=sQuery(id+"F34.wireOp",EDGE,"E28.0.right");Q21=makeQuery(id+"F9qVh1xIXOQniXD_4.1.FJxHqB9KzhM7FEk_4.1.F36.opFillet","BLEND_EDGE",EDGE,{"blendedFrom":[makeQuery(id+"F9qVh1xIXOQniXD_4.1.FJxHqB9KzhM7FEk_4.1.F35.boolean.opBoolean","COPY",EDGE,{"disambiguationData":[TD([makeQuery(id+"F28.boolean.opBoolean","COPY",FACE,{"derivedFrom":makeQuery(id+"F28.opExtrude","CAP_FACE",FACE,{"disambiguationData":[OSD([sQuery(id+"F27.wireOp",EDGE,"E16.0")])],"isStart":false})})])],"derivedFrom":makeQuery(id+"F9qVh1xIXOQniXD_4.1.FJxHqB9KzhM7FEk_4.1.F35.opExtrude","CAP_EDGE",EDGE,{"disambiguationData":[OSD([subQ0])],"isStart":false})}),makeQuery(id+"F1.opExtrude","SWEPT_FACE",FACE,{"disambiguationData":[OSD([sQuery(id+"F0.wireOp",EDGE,"E0.0")])]})],"blendedInto":[makeQuery(id+"F1.opExtrude","SWEPT_FACE",FACE,{"disambiguationData":[OSD([sQuery(id+"F0.wireOp",EDGE,"E0.0")])]})]});}
            var Q22;
            {var subQ0=sQuery(id+"F34.wireOp",EDGE,"E28.0.right");Q22=makeQuery(id+"F9qVh1xIXOQniXD_4.7.F36.opFillet","BLEND_EDGE",EDGE,{"blendedFrom":[makeQuery(id+"F9qVh1xIXOQniXD_4.7.F35.boolean.opBoolean","COPY",EDGE,{"disambiguationData":[TD([makeQuery(id+"F28.boolean.opBoolean","COPY",FACE,{"derivedFrom":makeQuery(id+"F28.opExtrude","CAP_FACE",FACE,{"disambiguationData":[OSD([sQuery(id+"F27.wireOp",EDGE,"E16.0")])],"isStart":false})})])],"derivedFrom":makeQuery(id+"F9qVh1xIXOQniXD_4.7.F35.opExtrude","CAP_EDGE",EDGE,{"disambiguationData":[OSD([subQ0])],"isStart":false})}),makeQuery(id+"F1.opExtrude","SWEPT_FACE",FACE,{"disambiguationData":[OSD([sQuery(id+"F0.wireOp",EDGE,"E0.0")])]})],"blendedInto":[makeQuery(id+"F1.opExtrude","SWEPT_FACE",FACE,{"disambiguationData":[OSD([sQuery(id+"F0.wireOp",EDGE,"E0.0")])]})]});}
            var Q23;
            Q23=makeQuery(id+"F1.opExtrude","SWEPT_EDGE",EDGE,{"disambiguationData":[OSD([sQuery(id+"F0.wireOp",EDGE,"E0.0"),sQuery(id+"F0.wireOp",EDGE,"E0.1")])]});
            var Q24;
            {var subQ0=sQuery(id+"F34.wireOp",EDGE,"E28.0.left");Q24=makeQuery(id+"F9qVh1xIXOQniXD_4.2.FJxHqB9KzhM7FEk_4.1.F36.opFillet","BLEND_EDGE",EDGE,{"blendedFrom":[makeQuery(id+"F9qVh1xIXOQniXD_4.2.FJxHqB9KzhM7FEk_4.1.F35.boolean.opBoolean","COPY",EDGE,{"disambiguationData":[TD([makeQuery(id+"F28.boolean.opBoolean","COPY",FACE,{"derivedFrom":makeQuery(id+"F28.opExtrude","CAP_FACE",FACE,{"disambiguationData":[OSD([sQuery(id+"F27.wireOp",EDGE,"E16.0")])],"isStart":false})})])],"derivedFrom":makeQuery(id+"F9qVh1xIXOQniXD_4.2.FJxHqB9KzhM7FEk_4.1.F35.opExtrude","CAP_EDGE",EDGE,{"disambiguationData":[OSD([subQ0])],"isStart":false})}),makeQuery(id+"F1.opExtrude","SWEPT_FACE",FACE,{"disambiguationData":[OSD([sQuery(id+"F0.wireOp",EDGE,"E0.1")])]})],"blendedInto":[makeQuery(id+"F1.opExtrude","SWEPT_FACE",FACE,{"disambiguationData":[OSD([sQuery(id+"F0.wireOp",EDGE,"E0.1")])]})]});}
            var Q25;
            {var subQ0=sQuery(id+"F34.wireOp",EDGE,"E28.0.right");Q25=makeQuery(id+"F9qVh1xIXOQniXD_4.6.F36.opFillet","BLEND_EDGE",EDGE,{"blendedFrom":[makeQuery(id+"F9qVh1xIXOQniXD_4.6.F35.boolean.opBoolean","COPY",EDGE,{"disambiguationData":[TD([makeQuery(id+"F28.boolean.opBoolean","COPY",FACE,{"derivedFrom":makeQuery(id+"F28.opExtrude","CAP_FACE",FACE,{"disambiguationData":[OSD([sQuery(id+"F27.wireOp",EDGE,"E16.0")])],"isStart":false})})])],"derivedFrom":makeQuery(id+"F9qVh1xIXOQniXD_4.6.F35.opExtrude","CAP_EDGE",EDGE,{"disambiguationData":[OSD([subQ0])],"isStart":false})}),makeQuery(id+"F1.opExtrude","SWEPT_FACE",FACE,{"disambiguationData":[OSD([sQuery(id+"F0.wireOp",EDGE,"E0.1")])]})],"blendedInto":[makeQuery(id+"F1.opExtrude","SWEPT_FACE",FACE,{"disambiguationData":[OSD([sQuery(id+"F0.wireOp",EDGE,"E0.1")])]})]});}
            fillet(context, id + "F62", {"entities" : qUnion([Q0, Q1, Q2, Q3, Q4, Q5, Q6, Q7, Q8, Q9, Q10, Q11, Q12, Q13, Q14, Q15, Q16, Q17, Q18, Q19, Q20, Q21, Q22, Q23, Q24, Q25]), "radius" : 5 * mm, "tangentPropagation" : true, "allowEdgeOverflow" : false});
        }
        {
            var Q0;
            Q0=makeQuery(id+"F33.opExtrude","SWEPT_EDGE",EDGE,{"disambiguationData":[OSD([sQuery(id+"F32.wireOp",EDGE,"E18.0"),sQuery(id+"F32.wireOp",EDGE,"E19.0")])]});
            var Q1;
            {var subQ0=sQuery(id+"F32.wireOp",EDGE,"E19.0");var subQ1=sQuery(id+"F34.wireOp",EDGE,"E28.0.startCap");var subQ2=sQuery(id+"F34.wireOp",EDGE,"E28.0.right");Q1=makeQuery(id+"F9qVh1xIXOQniXD_4.1.F36.opFillet","BLEND_EDGE",EDGE,{"blendedFrom":[makeQuery(id+"F9qVh1xIXOQniXD_4.1.F35.boolean.opBoolean","COPY",EDGE,{"disambiguationData":[TD([makeQuery(id+"F9qVh1xIXOQniXD_4.1.F35.opExtrude","SWEPT_FACE",FACE,{"disambiguationData":[OSD([subQ1])]})])],"derivedFrom":makeQuery(id+"F9qVh1xIXOQniXD_4.1.F35.opExtrude","CAP_EDGE",EDGE,{"disambiguationData":[OSD([subQ2])],"isStart":false})}),makeQuery(id+"F33.opExtrude","SWEPT_FACE",FACE,{"disambiguationData":[OSD([subQ0])]})],"blendedInto":[makeQuery(id+"F33.opExtrude","SWEPT_FACE",FACE,{"disambiguationData":[OSD([subQ0])]})]});}
            var Q2;
            {var subQ0=sQuery(id+"F32.wireOp",EDGE,"E19.0");var subQ1=sQuery(id+"F34.wireOp",EDGE,"E28.0.left");var subQ2=sQuery(id+"F34.wireOp",EDGE,"E28.0.startCap");Q2=makeQuery(id+"F9qVh1xIXOQniXD_4.7.FJxHqB9KzhM7FEk_4.1.F36.opFillet","BLEND_EDGE",EDGE,{"blendedFrom":[makeQuery(id+"F9qVh1xIXOQniXD_4.7.FJxHqB9KzhM7FEk_4.1.F35.boolean.opBoolean","COPY",EDGE,{"disambiguationData":[TD([makeQuery(id+"F9qVh1xIXOQniXD_4.7.FJxHqB9KzhM7FEk_4.1.F35.opExtrude","SWEPT_FACE",FACE,{"disambiguationData":[OSD([subQ2])]})])],"derivedFrom":makeQuery(id+"F9qVh1xIXOQniXD_4.7.FJxHqB9KzhM7FEk_4.1.F35.opExtrude","CAP_EDGE",EDGE,{"disambiguationData":[OSD([subQ1])],"isStart":false})}),makeQuery(id+"F33.opExtrude","SWEPT_FACE",FACE,{"disambiguationData":[OSD([subQ0])]})],"blendedInto":[makeQuery(id+"F33.opExtrude","SWEPT_FACE",FACE,{"disambiguationData":[OSD([subQ0])]})]});}
            var Q3;
            {var subQ0=sQuery(id+"F32.wireOp",EDGE,"E20.0");var subQ1=sQuery(id+"F34.wireOp",EDGE,"E28.0.right");var subQ2=sQuery(id+"F34.wireOp",EDGE,"E28.0.startCap");Q3=makeQuery(id+"F9qVh1xIXOQniXD_4.2.F36.opFillet","BLEND_EDGE",EDGE,{"blendedFrom":[makeQuery(id+"F9qVh1xIXOQniXD_4.2.F35.boolean.opBoolean","COPY",EDGE,{"disambiguationData":[TD([makeQuery(id+"F9qVh1xIXOQniXD_4.2.F35.opExtrude","SWEPT_FACE",FACE,{"disambiguationData":[OSD([subQ2])]})])],"derivedFrom":makeQuery(id+"F9qVh1xIXOQniXD_4.2.F35.opExtrude","CAP_EDGE",EDGE,{"disambiguationData":[OSD([subQ1])],"isStart":false})}),makeQuery(id+"F33.opExtrude","SWEPT_FACE",FACE,{"disambiguationData":[OSD([subQ0])]})],"blendedInto":[makeQuery(id+"F33.opExtrude","SWEPT_FACE",FACE,{"disambiguationData":[OSD([subQ0])]})]});}
            var Q4;
            {var subQ0=sQuery(id+"F32.wireOp",EDGE,"E20.0");var subQ1=sQuery(id+"F34.wireOp",EDGE,"E28.0.startCap");var subQ2=sQuery(id+"F34.wireOp",EDGE,"E28.0.left");Q4=makeQuery(id+"F9qVh1xIXOQniXD_4.6.FJxHqB9KzhM7FEk_4.1.F36.opFillet","BLEND_EDGE",EDGE,{"blendedFrom":[makeQuery(id+"F9qVh1xIXOQniXD_4.6.FJxHqB9KzhM7FEk_4.1.F35.boolean.opBoolean","COPY",EDGE,{"disambiguationData":[TD([makeQuery(id+"F9qVh1xIXOQniXD_4.6.FJxHqB9KzhM7FEk_4.1.F35.opExtrude","SWEPT_FACE",FACE,{"disambiguationData":[OSD([subQ1])]})])],"derivedFrom":makeQuery(id+"F9qVh1xIXOQniXD_4.6.FJxHqB9KzhM7FEk_4.1.F35.opExtrude","CAP_EDGE",EDGE,{"disambiguationData":[OSD([subQ2])],"isStart":false})}),makeQuery(id+"F33.opExtrude","SWEPT_FACE",FACE,{"disambiguationData":[OSD([subQ0])]})],"blendedInto":[makeQuery(id+"F33.opExtrude","SWEPT_FACE",FACE,{"disambiguationData":[OSD([subQ0])]})]});}
            var Q5;
            Q5=makeQuery(id+"F33.opExtrude","SWEPT_EDGE",EDGE,{"disambiguationData":[OSD([sQuery(id+"F32.wireOp",EDGE,"E20.0"),sQuery(id+"F32.wireOp",EDGE,"E24.0")])]});
            var Q6;
            {var subQ0=sQuery(id+"F32.wireOp",EDGE,"E18.0");var subQ1=sQuery(id+"F34.wireOp",EDGE,"E28.0.startCap");var subQ2=sQuery(id+"F34.wireOp",EDGE,"E28.0.left");Q6=makeQuery(id+"FJxHqB9KzhM7FEk_4.1.F36.opFillet","BLEND_EDGE",EDGE,{"blendedFrom":[makeQuery(id+"FJxHqB9KzhM7FEk_4.1.F35.boolean.opBoolean","COPY",EDGE,{"disambiguationData":[TD([makeQuery(id+"FJxHqB9KzhM7FEk_4.1.F35.opExtrude","SWEPT_FACE",FACE,{"disambiguationData":[OSD([subQ1])]})])],"derivedFrom":makeQuery(id+"FJxHqB9KzhM7FEk_4.1.F35.opExtrude","CAP_EDGE",EDGE,{"disambiguationData":[OSD([subQ2])],"isStart":false})}),makeQuery(id+"F33.opExtrude","SWEPT_FACE",FACE,{"disambiguationData":[OSD([subQ0])]})],"blendedInto":[makeQuery(id+"F33.opExtrude","SWEPT_FACE",FACE,{"disambiguationData":[OSD([subQ0])]})]});}
            var Q7;
            {var subQ0=sQuery(id+"F32.wireOp",EDGE,"E18.0");var subQ1=sQuery(id+"F34.wireOp",EDGE,"E28.0.startCap");var subQ2=sQuery(id+"F34.wireOp",EDGE,"E28.0.right");Q7=makeQuery(id+"F36.opFillet","BLEND_EDGE",EDGE,{"blendedFrom":[makeQuery(id+"F35.boolean.opBoolean","COPY",EDGE,{"disambiguationData":[TD([makeQuery(id+"F35.opExtrude","SWEPT_FACE",FACE,{"disambiguationData":[OSD([subQ1])]})])],"derivedFrom":makeQuery(id+"F35.opExtrude","CAP_EDGE",EDGE,{"disambiguationData":[OSD([subQ2])],"isStart":false})}),makeQuery(id+"F33.opExtrude","SWEPT_FACE",FACE,{"disambiguationData":[OSD([subQ0])]})],"blendedInto":[makeQuery(id+"F33.opExtrude","SWEPT_FACE",FACE,{"disambiguationData":[OSD([subQ0])]})]});}
            var Q8;
            {var subQ0=sQuery(id+"F32.wireOp",EDGE,"E24.0");var subQ1=sQuery(id+"F34.wireOp",EDGE,"E28.0.startCap");var subQ2=sQuery(id+"F34.wireOp",EDGE,"E28.0.right");Q8=makeQuery(id+"F9qVh1xIXOQniXD_4.3.F36.opFillet","BLEND_EDGE",EDGE,{"blendedFrom":[makeQuery(id+"F9qVh1xIXOQniXD_4.3.F35.boolean.opBoolean","COPY",EDGE,{"disambiguationData":[TD([makeQuery(id+"F9qVh1xIXOQniXD_4.3.F35.opExtrude","SWEPT_FACE",FACE,{"disambiguationData":[OSD([subQ1])]})])],"derivedFrom":makeQuery(id+"F9qVh1xIXOQniXD_4.3.F35.opExtrude","CAP_EDGE",EDGE,{"disambiguationData":[OSD([subQ2])],"isStart":false})}),makeQuery(id+"F33.opExtrude","SWEPT_FACE",FACE,{"disambiguationData":[OSD([subQ0])]})],"blendedInto":[makeQuery(id+"F33.opExtrude","SWEPT_FACE",FACE,{"disambiguationData":[OSD([subQ0])]})]});}
            var Q9;
            {var subQ0=sQuery(id+"F32.wireOp",EDGE,"E24.0");var subQ1=sQuery(id+"F34.wireOp",EDGE,"E28.0.startCap");var subQ2=sQuery(id+"F34.wireOp",EDGE,"E28.0.left");Q9=makeQuery(id+"F9qVh1xIXOQniXD_4.5.FJxHqB9KzhM7FEk_4.1.F36.opFillet","BLEND_EDGE",EDGE,{"blendedFrom":[makeQuery(id+"F9qVh1xIXOQniXD_4.5.FJxHqB9KzhM7FEk_4.1.F35.boolean.opBoolean","COPY",EDGE,{"disambiguationData":[TD([makeQuery(id+"F9qVh1xIXOQniXD_4.5.FJxHqB9KzhM7FEk_4.1.F35.opExtrude","SWEPT_FACE",FACE,{"disambiguationData":[OSD([subQ1])]})])],"derivedFrom":makeQuery(id+"F9qVh1xIXOQniXD_4.5.FJxHqB9KzhM7FEk_4.1.F35.opExtrude","CAP_EDGE",EDGE,{"disambiguationData":[OSD([subQ2])],"isStart":false})}),makeQuery(id+"F33.opExtrude","SWEPT_FACE",FACE,{"disambiguationData":[OSD([subQ0])]})],"blendedInto":[makeQuery(id+"F33.opExtrude","SWEPT_FACE",FACE,{"disambiguationData":[OSD([subQ0])]})]});}
            var Q10;
            Q10=makeQuery(id+"F33.opExtrude","SWEPT_EDGE",EDGE,{"disambiguationData":[OSD([sQuery(id+"F32.wireOp",EDGE,"E24.0"),sQuery(id+"F32.wireOp",EDGE,"E25.0")])]});
            var Q11;
            {var subQ0=sQuery(id+"F32.wireOp",EDGE,"E25.0");var subQ1=sQuery(id+"F34.wireOp",EDGE,"E28.0.startCap");var subQ2=sQuery(id+"F34.wireOp",EDGE,"E28.0.left");Q11=makeQuery(id+"F9qVh1xIXOQniXD_4.4.F36.opFillet","BLEND_EDGE",EDGE,{"blendedFrom":[makeQuery(id+"F9qVh1xIXOQniXD_4.4.F35.boolean.opBoolean","COPY",EDGE,{"disambiguationData":[TD([makeQuery(id+"F9qVh1xIXOQniXD_4.4.F35.opExtrude","SWEPT_FACE",FACE,{"disambiguationData":[OSD([subQ1])]})])],"derivedFrom":makeQuery(id+"F9qVh1xIXOQniXD_4.4.F35.opExtrude","CAP_EDGE",EDGE,{"disambiguationData":[OSD([subQ2])],"isStart":false})}),makeQuery(id+"F33.opExtrude","SWEPT_FACE",FACE,{"disambiguationData":[OSD([subQ0])]})],"blendedInto":[makeQuery(id+"F33.opExtrude","SWEPT_FACE",FACE,{"disambiguationData":[OSD([subQ0])]})]});}
            var Q12;
            {var subQ0=sQuery(id+"F32.wireOp",EDGE,"E25.0");var subQ1=sQuery(id+"F34.wireOp",EDGE,"E28.0.startCap");var subQ2=sQuery(id+"F34.wireOp",EDGE,"E28.0.right");Q12=makeQuery(id+"F9qVh1xIXOQniXD_4.4.FJxHqB9KzhM7FEk_4.1.F36.opFillet","BLEND_EDGE",EDGE,{"blendedFrom":[makeQuery(id+"F9qVh1xIXOQniXD_4.4.FJxHqB9KzhM7FEk_4.1.F35.boolean.opBoolean","COPY",EDGE,{"disambiguationData":[TD([makeQuery(id+"F9qVh1xIXOQniXD_4.4.FJxHqB9KzhM7FEk_4.1.F35.opExtrude","SWEPT_FACE",FACE,{"disambiguationData":[OSD([subQ1])]})])],"derivedFrom":makeQuery(id+"F9qVh1xIXOQniXD_4.4.FJxHqB9KzhM7FEk_4.1.F35.opExtrude","CAP_EDGE",EDGE,{"disambiguationData":[OSD([subQ2])],"isStart":false})}),makeQuery(id+"F33.opExtrude","SWEPT_FACE",FACE,{"disambiguationData":[OSD([subQ0])]})],"blendedInto":[makeQuery(id+"F33.opExtrude","SWEPT_FACE",FACE,{"disambiguationData":[OSD([subQ0])]})]});}
            var Q13;
            Q13=makeQuery(id+"F33.opExtrude","SWEPT_EDGE",EDGE,{"disambiguationData":[OSD([sQuery(id+"F32.wireOp",EDGE,"E23.0"),sQuery(id+"F32.wireOp",EDGE,"E25.0")])]});
            var Q14;
            Q14=makeQuery(id+"F9qVh1xIXOQniXD_4.5.F36.opFillet","BLEND_EDGE",EDGE,{"blendedFrom":[makeQuery(id+"F9qVh1xIXOQniXD_4.5.F35.boolean.opBoolean","COPY",EDGE,{"derivedFrom":makeQuery(id+"F9qVh1xIXOQniXD_4.5.F35.opExtrude","CAP_EDGE",EDGE,{"disambiguationData":[OSD([sQuery(id+"F34.wireOp",EDGE,"E28.0.startCap")])],"isStart":false})}),makeQuery(id+"F33.opExtrude","SWEPT_FACE",FACE,{"disambiguationData":[OSD([sQuery(id+"F32.wireOp",EDGE,"E23.0")])]})],"blendedInto":[makeQuery(id+"F33.opExtrude","SWEPT_FACE",FACE,{"disambiguationData":[OSD([sQuery(id+"F32.wireOp",EDGE,"E23.0")])]})]});
            var Q15;
            Q15=makeQuery(id+"F9qVh1xIXOQniXD_4.3.FJxHqB9KzhM7FEk_4.1.F36.opFillet","BLEND_EDGE",EDGE,{"blendedFrom":[makeQuery(id+"F9qVh1xIXOQniXD_4.3.FJxHqB9KzhM7FEk_4.1.F35.boolean.opBoolean","COPY",EDGE,{"derivedFrom":makeQuery(id+"F9qVh1xIXOQniXD_4.3.FJxHqB9KzhM7FEk_4.1.F35.opExtrude","CAP_EDGE",EDGE,{"disambiguationData":[OSD([sQuery(id+"F34.wireOp",EDGE,"E28.0.startCap")])],"isStart":false})}),makeQuery(id+"F33.opExtrude","SWEPT_FACE",FACE,{"disambiguationData":[OSD([sQuery(id+"F32.wireOp",EDGE,"E23.0")])]})],"blendedInto":[makeQuery(id+"F33.opExtrude","SWEPT_FACE",FACE,{"disambiguationData":[OSD([sQuery(id+"F32.wireOp",EDGE,"E23.0")])]})]});
            var Q16;
            Q16=makeQuery(id+"F33.opExtrude","SWEPT_EDGE",EDGE,{"disambiguationData":[OSD([sQuery(id+"F32.wireOp",EDGE,"E22.0"),sQuery(id+"F32.wireOp",EDGE,"E23.0")])]});
            var Q17;
            Q17=makeQuery(id+"F9qVh1xIXOQniXD_4.6.F36.opFillet","BLEND_EDGE",EDGE,{"blendedFrom":[makeQuery(id+"F9qVh1xIXOQniXD_4.6.F35.boolean.opBoolean","COPY",EDGE,{"derivedFrom":makeQuery(id+"F9qVh1xIXOQniXD_4.6.F35.opExtrude","CAP_EDGE",EDGE,{"disambiguationData":[OSD([sQuery(id+"F34.wireOp",EDGE,"E28.0.startCap")])],"isStart":false})}),makeQuery(id+"F33.opExtrude","SWEPT_FACE",FACE,{"disambiguationData":[OSD([sQuery(id+"F32.wireOp",EDGE,"E22.0")])]})],"blendedInto":[makeQuery(id+"F33.opExtrude","SWEPT_FACE",FACE,{"disambiguationData":[OSD([sQuery(id+"F32.wireOp",EDGE,"E22.0")])]})]});
            var Q18;
            Q18=makeQuery(id+"F9qVh1xIXOQniXD_4.2.FJxHqB9KzhM7FEk_4.1.F36.opFillet","BLEND_EDGE",EDGE,{"blendedFrom":[makeQuery(id+"F9qVh1xIXOQniXD_4.2.FJxHqB9KzhM7FEk_4.1.F35.boolean.opBoolean","COPY",EDGE,{"derivedFrom":makeQuery(id+"F9qVh1xIXOQniXD_4.2.FJxHqB9KzhM7FEk_4.1.F35.opExtrude","CAP_EDGE",EDGE,{"disambiguationData":[OSD([sQuery(id+"F34.wireOp",EDGE,"E28.0.startCap")])],"isStart":false})}),makeQuery(id+"F33.opExtrude","SWEPT_FACE",FACE,{"disambiguationData":[OSD([sQuery(id+"F32.wireOp",EDGE,"E22.0")])]})],"blendedInto":[makeQuery(id+"F33.opExtrude","SWEPT_FACE",FACE,{"disambiguationData":[OSD([sQuery(id+"F32.wireOp",EDGE,"E22.0")])]})]});
            var Q19;
            Q19=makeQuery(id+"F9qVh1xIXOQniXD_4.1.FJxHqB9KzhM7FEk_4.1.F36.opFillet","BLEND_EDGE",EDGE,{"blendedFrom":[makeQuery(id+"F9qVh1xIXOQniXD_4.1.FJxHqB9KzhM7FEk_4.1.F35.boolean.opBoolean","COPY",EDGE,{"derivedFrom":makeQuery(id+"F9qVh1xIXOQniXD_4.1.FJxHqB9KzhM7FEk_4.1.F35.opExtrude","CAP_EDGE",EDGE,{"disambiguationData":[OSD([sQuery(id+"F34.wireOp",EDGE,"E28.0.startCap")])],"isStart":false})}),makeQuery(id+"F33.opExtrude","SWEPT_FACE",FACE,{"disambiguationData":[OSD([sQuery(id+"F32.wireOp",EDGE,"E21.0")])]})],"blendedInto":[makeQuery(id+"F33.opExtrude","SWEPT_FACE",FACE,{"disambiguationData":[OSD([sQuery(id+"F32.wireOp",EDGE,"E21.0")])]})]});
            var Q20;
            Q20=makeQuery(id+"F9qVh1xIXOQniXD_4.7.F36.opFillet","BLEND_EDGE",EDGE,{"blendedFrom":[makeQuery(id+"F9qVh1xIXOQniXD_4.7.F35.boolean.opBoolean","COPY",EDGE,{"derivedFrom":makeQuery(id+"F9qVh1xIXOQniXD_4.7.F35.opExtrude","CAP_EDGE",EDGE,{"disambiguationData":[OSD([sQuery(id+"F34.wireOp",EDGE,"E28.0.startCap")])],"isStart":false})}),makeQuery(id+"F33.opExtrude","SWEPT_FACE",FACE,{"disambiguationData":[OSD([sQuery(id+"F32.wireOp",EDGE,"E21.0")])]})],"blendedInto":[makeQuery(id+"F33.opExtrude","SWEPT_FACE",FACE,{"disambiguationData":[OSD([sQuery(id+"F32.wireOp",EDGE,"E21.0")])]})]});
            fillet(context, id + "F63", {"entities" : qUnion([Q0, Q1, Q2, Q3, Q4, Q5, Q6, Q7, Q8, Q9, Q10, Q11, Q12, Q13, Q14, Q15, Q16, Q17, Q18, Q19, Q20]), "radius" : 5 * mm, "tangentPropagation" : true, "allowEdgeOverflow" : false});
        }
    });
